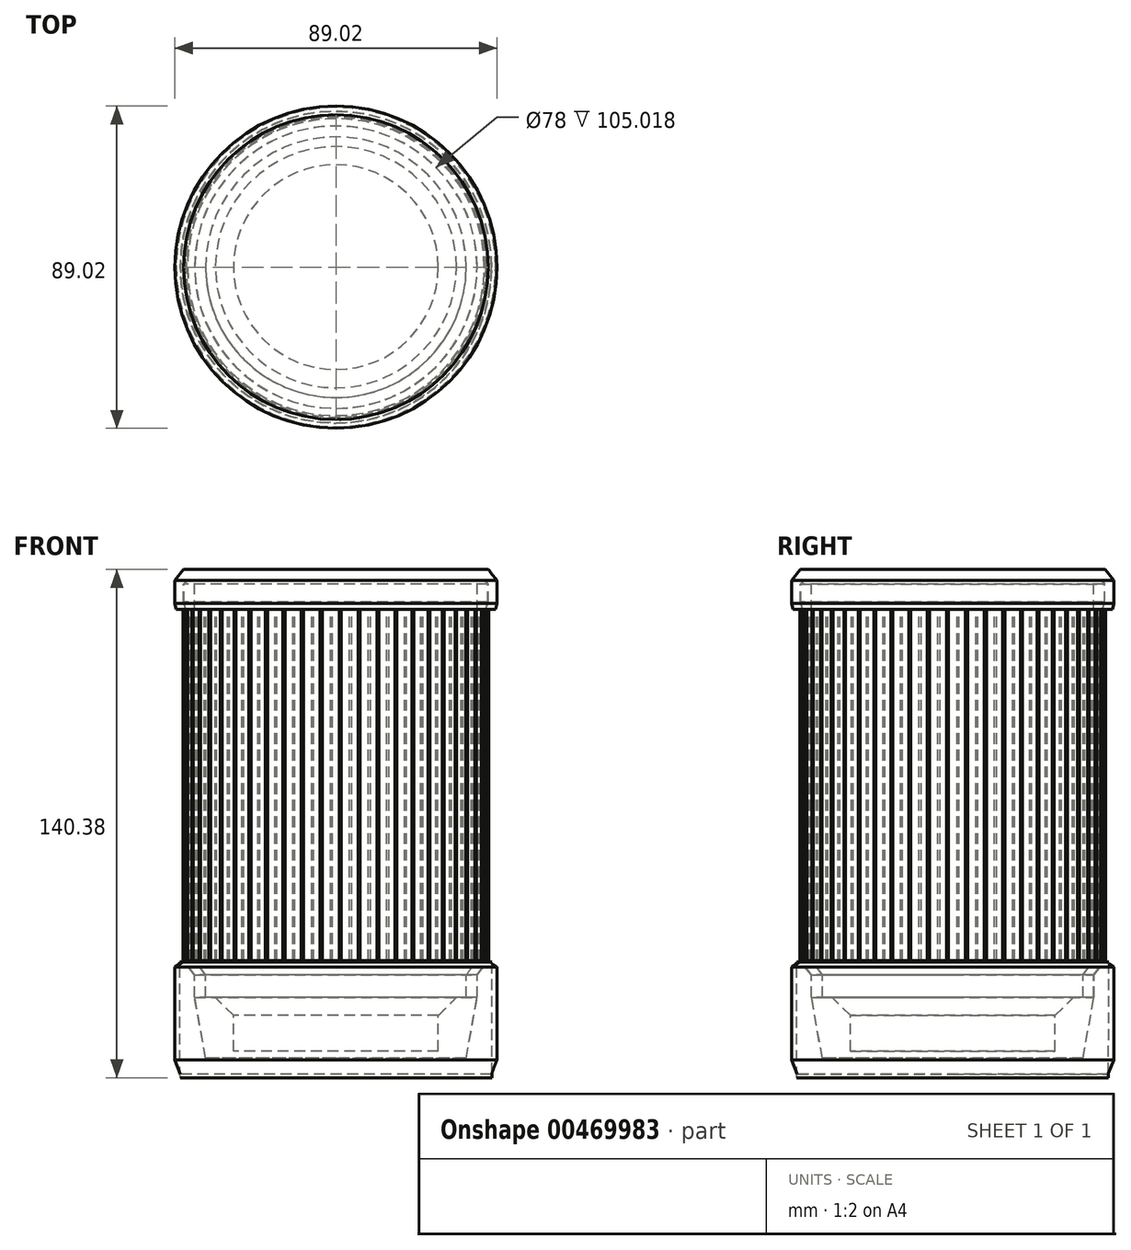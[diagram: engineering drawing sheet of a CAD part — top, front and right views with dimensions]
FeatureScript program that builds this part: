
annotation { "Feature Type Name" : "Feature", "Feature Type Description" : "" }
export const myFeature = defineFeature(function(context is Context, id is Id, definition is map)
    precondition{}
    {
        {
            var Q0;
            Q0=qCreatedBy(makeId("Front.planeOp"),FACE);
            var sketch = newSketch(context, id + "F0", { "sketchPlane" : qUnion([Q0])});
            skLineSegment(sketch, "E0", {"start": v(0, 0) * mm, "end": v(-28.3, 0) * mm});
            skLineSegment(sketch, "E1", {"start": v(-28.3, 0) * mm, "end": v(-28.3, 9.8) * mm});
            skLineSegment(sketch, "E2.bottom", {"start": v(0, 0) * mm, "end": v(-36, 0) * mm, "construction": true});
            skLineSegment(sketch, "E2.top", {"start": v(0, 21) * mm, "end": v(-36, 21) * mm, "construction": true});
            skLineSegment(sketch, "E2.left", {"start": v(0, 0) * mm, "end": v(0, 21) * mm, "construction": true});
            skLineSegment(sketch, "E2.right", {"start": v(-36, 0) * mm, "end": v(-36, 21) * mm, "construction": true});
            skLineSegment(sketch, "E3", {"start": v(-36, 21) * mm, "end": v(-36, 14.8) * mm});
            skLineSegment(sketch, "E4", {"start": v(-36, 14.8) * mm, "end": v(-33.3, 14.8) * mm});
            skLineSegment(sketch, "E5.bottom", {"start": v(0, 0) * mm, "end": v(-39, 0) * mm, "construction": true});
            skLineSegment(sketch, "E5.top", {"start": v(0, 130) * mm, "end": v(-39, 130) * mm, "construction": true});
            skLineSegment(sketch, "E5.left", {"start": v(0, 0) * mm, "end": v(0, 130) * mm, "construction": true});
            skLineSegment(sketch, "E5.right", {"start": v(-39, 0) * mm, "end": v(-39, 130) * mm, "construction": true});
            skLineSegment(sketch, "E6", {"start": v(-36, 21) * mm, "end": v(-39, 24.98) * mm});
            skLineSegment(sketch, "E7", {"start": v(-39, 24.98) * mm, "end": v(-39, 130) * mm});
            skLineSegment(sketch, "E8", {"start": v(-39, 130) * mm, "end": v(-42, 130) * mm});
            skLineSegment(sketch, "E9", {"start": v(-42, 130) * mm, "end": v(-42, 124) * mm});
            skLineSegment(sketch, "E10.bottom", {"start": v(-39, 130) * mm, "end": v(-41.4, 130) * mm, "construction": true});
            skLineSegment(sketch, "E10.top", {"start": v(-39, 122) * mm, "end": v(-41.4, 122) * mm, "construction": true});
            skLineSegment(sketch, "E10.left", {"start": v(-39, 130) * mm, "end": v(-39, 122) * mm, "construction": true});
            skLineSegment(sketch, "E10.right", {"start": v(-41.4, 130) * mm, "end": v(-41.4, 122) * mm, "construction": true});
            skLineSegment(sketch, "E11", {"start": v(-42, 124) * mm, "end": v(-41.4, 122) * mm});
            skLineSegment(sketch, "E12", {"start": v(-42, 122) * mm, "end": v(-42, 24.98) * mm});
            skLineSegment(sketch, "E13", {"start": v(-42, 24.98) * mm, "end": v(-39, 21) * mm});
            skLineSegment(sketch, "E14", {"start": v(-39, 21) * mm, "end": v(-39, 14.8) * mm});
            skLineSegment(sketch, "E15", {"start": v(-36, 17.9) * mm, "end": v(-39, 17.9) * mm, "construction": true});
            skLineSegment(sketch, "E16", {"start": v(0, 0) * mm, "end": v(0, -2) * mm});
            skLineSegment(sketch, "E17", {"start": v(0, -2) * mm, "end": v(-28.3, -2) * mm});
            skLineSegment(sketch, "E18", {"start": v(-39, 14.8) * mm, "end": v(-36, -2) * mm});
            skLineSegment(sketch, "E19", {"start": v(-36, -2) * mm, "end": v(-28.3, -2) * mm});
            skLineSegment(sketch, "E20", {"start": v(-33.3, 14.8) * mm, "end": v(-28.3, 9.8) * mm});
            skLineSegment(sketch, "E21", {"start": v(-42, 122) * mm, "end": v(-41.4, 122) * mm});
            skSolve(sketch);
        }
        {
            var Q0;
            Q0=makeQuery(id+"F0.imprint","IMPRINT",FACE,{"disambiguationData":[TD([[makeQuery(id+"F0.imprint","IMPRINT",EDGE,{"derivedFrom":sQuery(id+"F0.wireOp",EDGE,"E0")}),1.0]])]});
            var Q1;
            Q1=sQuery(id+"F0.wireOp",EDGE,"E16");
            revolve(context, id + "F1", {"entities" : qUnion([Q0]), "axis" : qUnion([Q1]), "revolveType" : RevolveType.FULL});
        }
        {
            var Q0;
            Q0=makeQuery(id+"F1.opRevolve","SWEPT_FACE",FACE,{"disambiguationData":[OSD([sQuery(id+"F0.wireOp",EDGE,"E21")])]});
            var sketch = newSketch(context, id + "F2", { "sketchPlane" : qUnion([Q0])});
            skCircle(sketch, "E22", {"center": v(36.08, -21.5) * mm, "radius": 0.29 * mm});
            skCircle(sketch, "E23.1.0", {"center": v(38.5, -16.8) * mm, "radius": 0.29 * mm});
            skCircle(sketch, "E23.2.0", {"center": v(40.3, -11.84) * mm, "radius": 0.29 * mm});
            skCircle(sketch, "E23.3.0", {"center": v(41.46, -6.7) * mm, "radius": 0.29 * mm});
            skCircle(sketch, "E23.4.0", {"center": v(41.97, -1.45) * mm, "radius": 0.29 * mm});
            skCircle(sketch, "E23.5.0", {"center": v(41.83, 3.82) * mm, "radius": 0.29 * mm});
            skCircle(sketch, "E23.6.0", {"center": v(41.02, 9.03) * mm, "radius": 0.29 * mm});
            skCircle(sketch, "E23.7.0", {"center": v(39.56, 14.1) * mm, "radius": 0.29 * mm});
            skCircle(sketch, "E23.8.0", {"center": v(37.48, 18.95) * mm, "radius": 0.29 * mm});
            skCircle(sketch, "E23.9.0", {"center": v(34.81, 23.5) * mm, "radius": 0.29 * mm});
            skCircle(sketch, "E23.10.0", {"center": v(31.6, 27.68) * mm, "radius": 0.29 * mm});
            skCircle(sketch, "E23.11.0", {"center": v(27.87, 31.42) * mm, "radius": 0.29 * mm});
            skCircle(sketch, "E23.12.0", {"center": v(23.72, 34.66) * mm, "radius": 0.29 * mm});
            skCircle(sketch, "E23.13.0", {"center": v(19.19, 37.36) * mm, "radius": 0.29 * mm});
            skCircle(sketch, "E23.14.0", {"center": v(14.35, 39.47) * mm, "radius": 0.29 * mm});
            skCircle(sketch, "E23.15.0", {"center": v(9.3, 40.96) * mm, "radius": 0.29 * mm});
            skCircle(sketch, "E23.16.0", {"center": v(4.08, 41.8) * mm, "radius": 0.29 * mm});
            skCircle(sketch, "E23.17.0", {"center": v(-1.19, 41.98) * mm, "radius": 0.29 * mm});
            skCircle(sketch, "E23.18.0", {"center": v(-6.44, 41.5) * mm, "radius": 0.29 * mm});
            skCircle(sketch, "E23.19.0", {"center": v(-11.6, 40.37) * mm, "radius": 0.29 * mm});
            skCircle(sketch, "E23.20.0", {"center": v(-16.56, 38.6) * mm, "radius": 0.29 * mm});
            skCircle(sketch, "E23.21.0", {"center": v(-21.27, 36.22) * mm, "radius": 0.29 * mm});
            skCircle(sketch, "E23.22.0", {"center": v(-25.64, 33.27) * mm, "radius": 0.29 * mm});
            skCircle(sketch, "E23.23.0", {"center": v(-29.6, 29.8) * mm, "radius": 0.29 * mm});
            skCircle(sketch, "E23.24.0", {"center": v(-33.1, 25.85) * mm, "radius": 0.29 * mm});
            skCircle(sketch, "E23.25.0", {"center": v(-36.08, 21.5) * mm, "radius": 0.29 * mm});
            skCircle(sketch, "E23.26.0", {"center": v(-38.5, 16.8) * mm, "radius": 0.29 * mm});
            skCircle(sketch, "E23.27.0", {"center": v(-40.3, 11.84) * mm, "radius": 0.29 * mm});
            skCircle(sketch, "E23.28.0", {"center": v(-41.46, 6.7) * mm, "radius": 0.29 * mm});
            skCircle(sketch, "E23.29.0", {"center": v(-41.97, 1.45) * mm, "radius": 0.29 * mm});
            skCircle(sketch, "E23.30.0", {"center": v(-41.83, -3.82) * mm, "radius": 0.29 * mm});
            skCircle(sketch, "E23.31.0", {"center": v(-41.02, -9.03) * mm, "radius": 0.29 * mm});
            skCircle(sketch, "E23.32.0", {"center": v(-39.56, -14.1) * mm, "radius": 0.29 * mm});
            skCircle(sketch, "E23.33.0", {"center": v(-37.48, -18.95) * mm, "radius": 0.29 * mm});
            skCircle(sketch, "E23.34.0", {"center": v(-34.81, -23.5) * mm, "radius": 0.29 * mm});
            skCircle(sketch, "E23.35.0", {"center": v(-31.6, -27.68) * mm, "radius": 0.29 * mm});
            skCircle(sketch, "E23.36.0", {"center": v(-27.87, -31.42) * mm, "radius": 0.29 * mm});
            skCircle(sketch, "E23.37.0", {"center": v(-23.72, -34.66) * mm, "radius": 0.29 * mm});
            skCircle(sketch, "E23.38.0", {"center": v(-19.19, -37.36) * mm, "radius": 0.29 * mm});
            skCircle(sketch, "E23.39.0", {"center": v(-14.35, -39.47) * mm, "radius": 0.29 * mm});
            skCircle(sketch, "E23.40.0", {"center": v(-9.3, -40.96) * mm, "radius": 0.29 * mm});
            skCircle(sketch, "E23.41.0", {"center": v(-4.08, -41.8) * mm, "radius": 0.29 * mm});
            skCircle(sketch, "E23.42.0", {"center": v(1.19, -41.98) * mm, "radius": 0.29 * mm});
            skCircle(sketch, "E23.43.0", {"center": v(6.44, -41.5) * mm, "radius": 0.29 * mm});
            skCircle(sketch, "E23.44.0", {"center": v(11.6, -40.37) * mm, "radius": 0.29 * mm});
            skCircle(sketch, "E23.45.0", {"center": v(16.56, -38.6) * mm, "radius": 0.29 * mm});
            skCircle(sketch, "E23.46.0", {"center": v(21.27, -36.22) * mm, "radius": 0.29 * mm});
            skCircle(sketch, "E23.47.0", {"center": v(25.64, -33.27) * mm, "radius": 0.29 * mm});
            skCircle(sketch, "E23.48.0", {"center": v(29.6, -29.8) * mm, "radius": 0.29 * mm});
            skCircle(sketch, "E23.49.0", {"center": v(33.1, -25.85) * mm, "radius": 0.29 * mm});
            skPoint(sketch, "E23.center", {"position": v(0, 0) * mm});
            skSolve(sketch);
        }
        {
            var Q0;
            {var subQ0=sQuery(id+"F2.wireOp",EDGE,"E23.46.0");var subQ1=makeQuery(id+"F1.opRevolve","SWEPT_EDGE",EDGE,{"disambiguationData":[OSD([sQuery(id+"F0.wireOp",EDGE,"E12"),sQuery(id+"F0.wireOp",EDGE,"E21")])]});var subQ2=makeQuery(id+"F2.imprint","INTERSECT",VERTEX,{"disambiguationData":[OD(0.0)],"derivedFrom":[subQ1,subQ0]});Q0=makeQuery(id+"F2.imprint","IMPRINT",FACE,{"disambiguationData":[TD([[makeQuery(id+"F2.imprint","IMPRINT",EDGE,{"disambiguationData":[TD([[subQ2,1.0]])],"derivedFrom":subQ0}),1.0]])]});}
            var Q1;
            {var subQ0=sQuery(id+"F2.wireOp",EDGE,"E23.46.0");var subQ1=makeQuery(id+"F1.opRevolve","SWEPT_EDGE",EDGE,{"disambiguationData":[OSD([sQuery(id+"F0.wireOp",EDGE,"E12"),sQuery(id+"F0.wireOp",EDGE,"E21")])]});var subQ2=makeQuery(id+"F2.imprint","INTERSECT",VERTEX,{"disambiguationData":[OD(0.0)],"derivedFrom":[subQ1,subQ0]});Q1=makeQuery(id+"F2.imprint","IMPRINT",FACE,{"disambiguationData":[TD([[makeQuery(id+"F2.imprint","IMPRINT",EDGE,{"disambiguationData":[TD([[subQ2,-1.0]])],"derivedFrom":subQ0}),1.0]])]});}
            var Q2;
            {var subQ0=sQuery(id+"F2.wireOp",EDGE,"E23.47.0");var subQ1=makeQuery(id+"F1.opRevolve","SWEPT_EDGE",EDGE,{"disambiguationData":[OSD([sQuery(id+"F0.wireOp",EDGE,"E12"),sQuery(id+"F0.wireOp",EDGE,"E21")])]});var subQ2=makeQuery(id+"F2.imprint","INTERSECT",VERTEX,{"disambiguationData":[OD(0.0)],"derivedFrom":[subQ1,subQ0]});Q2=makeQuery(id+"F2.imprint","IMPRINT",FACE,{"disambiguationData":[TD([[makeQuery(id+"F2.imprint","IMPRINT",EDGE,{"disambiguationData":[TD([[subQ2,-1.0]])],"derivedFrom":subQ0}),1.0]])]});}
            var Q3;
            {var subQ0=sQuery(id+"F2.wireOp",EDGE,"E23.47.0");var subQ1=makeQuery(id+"F1.opRevolve","SWEPT_EDGE",EDGE,{"disambiguationData":[OSD([sQuery(id+"F0.wireOp",EDGE,"E12"),sQuery(id+"F0.wireOp",EDGE,"E21")])]});var subQ2=makeQuery(id+"F2.imprint","INTERSECT",VERTEX,{"disambiguationData":[OD(0.0)],"derivedFrom":[subQ1,subQ0]});Q3=makeQuery(id+"F2.imprint","IMPRINT",FACE,{"disambiguationData":[TD([[makeQuery(id+"F2.imprint","IMPRINT",EDGE,{"disambiguationData":[TD([[subQ2,1.0]])],"derivedFrom":subQ0}),1.0]])]});}
            var Q4;
            {var subQ0=sQuery(id+"F2.wireOp",EDGE,"E23.48.0");var subQ1=makeQuery(id+"F1.opRevolve","SWEPT_EDGE",EDGE,{"disambiguationData":[OSD([sQuery(id+"F0.wireOp",EDGE,"E12"),sQuery(id+"F0.wireOp",EDGE,"E21")])]});var subQ2=makeQuery(id+"F2.imprint","INTERSECT",VERTEX,{"disambiguationData":[OD(0.0)],"derivedFrom":[subQ1,subQ0]});Q4=makeQuery(id+"F2.imprint","IMPRINT",FACE,{"disambiguationData":[TD([[makeQuery(id+"F2.imprint","IMPRINT",EDGE,{"disambiguationData":[TD([[subQ2,-1.0]])],"derivedFrom":subQ0}),1.0]])]});}
            var Q5;
            {var subQ0=sQuery(id+"F2.wireOp",EDGE,"E23.48.0");var subQ1=makeQuery(id+"F1.opRevolve","SWEPT_EDGE",EDGE,{"disambiguationData":[OSD([sQuery(id+"F0.wireOp",EDGE,"E12"),sQuery(id+"F0.wireOp",EDGE,"E21")])]});var subQ2=makeQuery(id+"F2.imprint","INTERSECT",VERTEX,{"disambiguationData":[OD(0.0)],"derivedFrom":[subQ1,subQ0]});Q5=makeQuery(id+"F2.imprint","IMPRINT",FACE,{"disambiguationData":[TD([[makeQuery(id+"F2.imprint","IMPRINT",EDGE,{"disambiguationData":[TD([[subQ2,1.0]])],"derivedFrom":subQ0}),1.0]])]});}
            var Q6;
            {var subQ0=sQuery(id+"F2.wireOp",EDGE,"E23.49.0");var subQ1=makeQuery(id+"F1.opRevolve","SWEPT_EDGE",EDGE,{"disambiguationData":[OSD([sQuery(id+"F0.wireOp",EDGE,"E12"),sQuery(id+"F0.wireOp",EDGE,"E21")])]});var subQ2=makeQuery(id+"F2.imprint","INTERSECT",VERTEX,{"disambiguationData":[OD(0.0)],"derivedFrom":[subQ1,subQ0]});Q6=makeQuery(id+"F2.imprint","IMPRINT",FACE,{"disambiguationData":[TD([[makeQuery(id+"F2.imprint","IMPRINT",EDGE,{"disambiguationData":[TD([[subQ2,-1.0]])],"derivedFrom":subQ0}),1.0]])]});}
            var Q7;
            {var subQ0=sQuery(id+"F2.wireOp",EDGE,"E23.49.0");var subQ1=makeQuery(id+"F1.opRevolve","SWEPT_EDGE",EDGE,{"disambiguationData":[OSD([sQuery(id+"F0.wireOp",EDGE,"E12"),sQuery(id+"F0.wireOp",EDGE,"E21")])]});var subQ2=makeQuery(id+"F2.imprint","INTERSECT",VERTEX,{"disambiguationData":[OD(0.0)],"derivedFrom":[subQ1,subQ0]});Q7=makeQuery(id+"F2.imprint","IMPRINT",FACE,{"disambiguationData":[TD([[makeQuery(id+"F2.imprint","IMPRINT",EDGE,{"disambiguationData":[TD([[subQ2,1.0]])],"derivedFrom":subQ0}),1.0]])]});}
            var Q8;
            {var subQ0=sQuery(id+"F2.wireOp",EDGE,"E22");var subQ1=makeQuery(id+"F1.opRevolve","SWEPT_EDGE",EDGE,{"disambiguationData":[OSD([sQuery(id+"F0.wireOp",EDGE,"E12"),sQuery(id+"F0.wireOp",EDGE,"E21")])]});var subQ2=makeQuery(id+"F2.imprint","INTERSECT",VERTEX,{"disambiguationData":[OD(0.0)],"derivedFrom":[subQ1,subQ0]});Q8=makeQuery(id+"F2.imprint","IMPRINT",FACE,{"disambiguationData":[TD([[makeQuery(id+"F2.imprint","IMPRINT",EDGE,{"disambiguationData":[TD([[subQ2,-1.0]])],"derivedFrom":subQ0}),1.0]])]});}
            var Q9;
            {var subQ0=sQuery(id+"F2.wireOp",EDGE,"E22");var subQ1=makeQuery(id+"F1.opRevolve","SWEPT_EDGE",EDGE,{"disambiguationData":[OSD([sQuery(id+"F0.wireOp",EDGE,"E12"),sQuery(id+"F0.wireOp",EDGE,"E21")])]});var subQ2=makeQuery(id+"F2.imprint","INTERSECT",VERTEX,{"disambiguationData":[OD(0.0)],"derivedFrom":[subQ1,subQ0]});Q9=makeQuery(id+"F2.imprint","IMPRINT",FACE,{"disambiguationData":[TD([[makeQuery(id+"F2.imprint","IMPRINT",EDGE,{"disambiguationData":[TD([[subQ2,1.0]])],"derivedFrom":subQ0}),1.0]])]});}
            var Q10;
            {var subQ0=sQuery(id+"F2.wireOp",EDGE,"E23.1.0");var subQ1=makeQuery(id+"F1.opRevolve","SWEPT_EDGE",EDGE,{"disambiguationData":[OSD([sQuery(id+"F0.wireOp",EDGE,"E12"),sQuery(id+"F0.wireOp",EDGE,"E21")])]});var subQ2=makeQuery(id+"F2.imprint","INTERSECT",VERTEX,{"disambiguationData":[OD(0.0)],"derivedFrom":[subQ1,subQ0]});Q10=makeQuery(id+"F2.imprint","IMPRINT",FACE,{"disambiguationData":[TD([[makeQuery(id+"F2.imprint","IMPRINT",EDGE,{"disambiguationData":[TD([[subQ2,-1.0]])],"derivedFrom":subQ0}),1.0]])]});}
            var Q11;
            {var subQ0=sQuery(id+"F2.wireOp",EDGE,"E23.1.0");var subQ1=makeQuery(id+"F1.opRevolve","SWEPT_EDGE",EDGE,{"disambiguationData":[OSD([sQuery(id+"F0.wireOp",EDGE,"E12"),sQuery(id+"F0.wireOp",EDGE,"E21")])]});var subQ2=makeQuery(id+"F2.imprint","INTERSECT",VERTEX,{"disambiguationData":[OD(0.0)],"derivedFrom":[subQ1,subQ0]});Q11=makeQuery(id+"F2.imprint","IMPRINT",FACE,{"disambiguationData":[TD([[makeQuery(id+"F2.imprint","IMPRINT",EDGE,{"disambiguationData":[TD([[subQ2,1.0]])],"derivedFrom":subQ0}),1.0]])]});}
            var Q12;
            {var subQ0=sQuery(id+"F2.wireOp",EDGE,"E23.2.0");var subQ1=makeQuery(id+"F1.opRevolve","SWEPT_EDGE",EDGE,{"disambiguationData":[OSD([sQuery(id+"F0.wireOp",EDGE,"E12"),sQuery(id+"F0.wireOp",EDGE,"E21")])]});var subQ2=makeQuery(id+"F2.imprint","INTERSECT",VERTEX,{"disambiguationData":[OD(0.0)],"derivedFrom":[subQ1,subQ0]});Q12=makeQuery(id+"F2.imprint","IMPRINT",FACE,{"disambiguationData":[TD([[makeQuery(id+"F2.imprint","IMPRINT",EDGE,{"disambiguationData":[TD([[subQ2,1.0]])],"derivedFrom":subQ0}),1.0]])]});}
            var Q13;
            {var subQ0=sQuery(id+"F2.wireOp",EDGE,"E23.2.0");var subQ1=makeQuery(id+"F1.opRevolve","SWEPT_EDGE",EDGE,{"disambiguationData":[OSD([sQuery(id+"F0.wireOp",EDGE,"E12"),sQuery(id+"F0.wireOp",EDGE,"E21")])]});var subQ2=makeQuery(id+"F2.imprint","INTERSECT",VERTEX,{"disambiguationData":[OD(0.0)],"derivedFrom":[subQ1,subQ0]});Q13=makeQuery(id+"F2.imprint","IMPRINT",FACE,{"disambiguationData":[TD([[makeQuery(id+"F2.imprint","IMPRINT",EDGE,{"disambiguationData":[TD([[subQ2,-1.0]])],"derivedFrom":subQ0}),1.0]])]});}
            var Q14;
            {var subQ0=sQuery(id+"F2.wireOp",EDGE,"E23.3.0");var subQ1=makeQuery(id+"F1.opRevolve","SWEPT_EDGE",EDGE,{"disambiguationData":[OSD([sQuery(id+"F0.wireOp",EDGE,"E12"),sQuery(id+"F0.wireOp",EDGE,"E21")])]});var subQ2=makeQuery(id+"F2.imprint","INTERSECT",VERTEX,{"disambiguationData":[OD(0.0)],"derivedFrom":[subQ1,subQ0]});Q14=makeQuery(id+"F2.imprint","IMPRINT",FACE,{"disambiguationData":[TD([[makeQuery(id+"F2.imprint","IMPRINT",EDGE,{"disambiguationData":[TD([[subQ2,1.0]])],"derivedFrom":subQ0}),1.0]])]});}
            var Q15;
            {var subQ0=sQuery(id+"F2.wireOp",EDGE,"E23.3.0");var subQ1=makeQuery(id+"F1.opRevolve","SWEPT_EDGE",EDGE,{"disambiguationData":[OSD([sQuery(id+"F0.wireOp",EDGE,"E12"),sQuery(id+"F0.wireOp",EDGE,"E21")])]});var subQ2=makeQuery(id+"F2.imprint","INTERSECT",VERTEX,{"disambiguationData":[OD(0.0)],"derivedFrom":[subQ1,subQ0]});Q15=makeQuery(id+"F2.imprint","IMPRINT",FACE,{"disambiguationData":[TD([[makeQuery(id+"F2.imprint","IMPRINT",EDGE,{"disambiguationData":[TD([[subQ2,-1.0]])],"derivedFrom":subQ0}),1.0]])]});}
            var Q16;
            {var subQ0=sQuery(id+"F2.wireOp",EDGE,"E23.4.0");var subQ1=makeQuery(id+"F1.opRevolve","SWEPT_EDGE",EDGE,{"disambiguationData":[OSD([sQuery(id+"F0.wireOp",EDGE,"E12"),sQuery(id+"F0.wireOp",EDGE,"E21")])]});var subQ2=makeQuery(id+"F2.imprint","INTERSECT",VERTEX,{"disambiguationData":[OD(0.0)],"derivedFrom":[subQ1,subQ0]});Q16=makeQuery(id+"F2.imprint","IMPRINT",FACE,{"disambiguationData":[TD([[makeQuery(id+"F2.imprint","IMPRINT",EDGE,{"disambiguationData":[TD([[subQ2,-1.0]])],"derivedFrom":subQ0}),1.0]])]});}
            var Q17;
            {var subQ0=sQuery(id+"F2.wireOp",EDGE,"E23.5.0");var subQ1=makeQuery(id+"F1.opRevolve","SWEPT_EDGE",EDGE,{"disambiguationData":[OSD([sQuery(id+"F0.wireOp",EDGE,"E12"),sQuery(id+"F0.wireOp",EDGE,"E21")])]});var subQ2=makeQuery(id+"F2.imprint","INTERSECT",VERTEX,{"disambiguationData":[OD(0.0)],"derivedFrom":[subQ1,subQ0]});Q17=makeQuery(id+"F2.imprint","IMPRINT",FACE,{"disambiguationData":[TD([[makeQuery(id+"F2.imprint","IMPRINT",EDGE,{"disambiguationData":[TD([[subQ2,-1.0]])],"derivedFrom":subQ0}),1.0]])]});}
            var Q18;
            {var subQ0=sQuery(id+"F2.wireOp",EDGE,"E23.9.0");var subQ1=makeQuery(id+"F1.opRevolve","SWEPT_EDGE",EDGE,{"disambiguationData":[OSD([sQuery(id+"F0.wireOp",EDGE,"E12"),sQuery(id+"F0.wireOp",EDGE,"E21")])]});var subQ2=makeQuery(id+"F2.imprint","INTERSECT",VERTEX,{"disambiguationData":[OD(0.0)],"derivedFrom":[subQ1,subQ0]});Q18=makeQuery(id+"F2.imprint","IMPRINT",FACE,{"disambiguationData":[TD([[makeQuery(id+"F2.imprint","IMPRINT",EDGE,{"disambiguationData":[TD([[subQ2,1.0]])],"derivedFrom":subQ0}),1.0]])]});}
            var Q19;
            {var subQ0=sQuery(id+"F2.wireOp",EDGE,"E23.8.0");var subQ1=makeQuery(id+"F1.opRevolve","SWEPT_EDGE",EDGE,{"disambiguationData":[OSD([sQuery(id+"F0.wireOp",EDGE,"E12"),sQuery(id+"F0.wireOp",EDGE,"E21")])]});var subQ2=makeQuery(id+"F2.imprint","INTERSECT",VERTEX,{"disambiguationData":[OD(0.0)],"derivedFrom":[subQ1,subQ0]});Q19=makeQuery(id+"F2.imprint","IMPRINT",FACE,{"disambiguationData":[TD([[makeQuery(id+"F2.imprint","IMPRINT",EDGE,{"disambiguationData":[TD([[subQ2,1.0]])],"derivedFrom":subQ0}),1.0]])]});}
            var Q20;
            {var subQ0=sQuery(id+"F2.wireOp",EDGE,"E23.7.0");var subQ1=makeQuery(id+"F1.opRevolve","SWEPT_EDGE",EDGE,{"disambiguationData":[OSD([sQuery(id+"F0.wireOp",EDGE,"E12"),sQuery(id+"F0.wireOp",EDGE,"E21")])]});var subQ2=makeQuery(id+"F2.imprint","INTERSECT",VERTEX,{"disambiguationData":[OD(0.0)],"derivedFrom":[subQ1,subQ0]});Q20=makeQuery(id+"F2.imprint","IMPRINT",FACE,{"disambiguationData":[TD([[makeQuery(id+"F2.imprint","IMPRINT",EDGE,{"disambiguationData":[TD([[subQ2,-1.0]])],"derivedFrom":subQ0}),1.0]])]});}
            var Q21;
            {var subQ0=sQuery(id+"F2.wireOp",EDGE,"E23.6.0");var subQ1=makeQuery(id+"F1.opRevolve","SWEPT_EDGE",EDGE,{"disambiguationData":[OSD([sQuery(id+"F0.wireOp",EDGE,"E12"),sQuery(id+"F0.wireOp",EDGE,"E21")])]});var subQ2=makeQuery(id+"F2.imprint","INTERSECT",VERTEX,{"disambiguationData":[OD(0.0)],"derivedFrom":[subQ1,subQ0]});Q21=makeQuery(id+"F2.imprint","IMPRINT",FACE,{"disambiguationData":[TD([[makeQuery(id+"F2.imprint","IMPRINT",EDGE,{"disambiguationData":[TD([[subQ2,-1.0]])],"derivedFrom":subQ0}),1.0]])]});}
            var Q22;
            {var subQ0=sQuery(id+"F2.wireOp",EDGE,"E23.7.0");var subQ1=makeQuery(id+"F1.opRevolve","SWEPT_EDGE",EDGE,{"disambiguationData":[OSD([sQuery(id+"F0.wireOp",EDGE,"E12"),sQuery(id+"F0.wireOp",EDGE,"E21")])]});var subQ2=makeQuery(id+"F2.imprint","INTERSECT",VERTEX,{"disambiguationData":[OD(0.0)],"derivedFrom":[subQ1,subQ0]});Q22=makeQuery(id+"F2.imprint","IMPRINT",FACE,{"disambiguationData":[TD([[makeQuery(id+"F2.imprint","IMPRINT",EDGE,{"disambiguationData":[TD([[subQ2,1.0]])],"derivedFrom":subQ0}),1.0]])]});}
            var Q23;
            {var subQ0=sQuery(id+"F2.wireOp",EDGE,"E23.8.0");var subQ1=makeQuery(id+"F1.opRevolve","SWEPT_EDGE",EDGE,{"disambiguationData":[OSD([sQuery(id+"F0.wireOp",EDGE,"E12"),sQuery(id+"F0.wireOp",EDGE,"E21")])]});var subQ2=makeQuery(id+"F2.imprint","INTERSECT",VERTEX,{"disambiguationData":[OD(0.0)],"derivedFrom":[subQ1,subQ0]});Q23=makeQuery(id+"F2.imprint","IMPRINT",FACE,{"disambiguationData":[TD([[makeQuery(id+"F2.imprint","IMPRINT",EDGE,{"disambiguationData":[TD([[subQ2,-1.0]])],"derivedFrom":subQ0}),1.0]])]});}
            var Q24;
            {var subQ0=sQuery(id+"F2.wireOp",EDGE,"E23.6.0");var subQ1=makeQuery(id+"F1.opRevolve","SWEPT_EDGE",EDGE,{"disambiguationData":[OSD([sQuery(id+"F0.wireOp",EDGE,"E12"),sQuery(id+"F0.wireOp",EDGE,"E21")])]});var subQ2=makeQuery(id+"F2.imprint","INTERSECT",VERTEX,{"disambiguationData":[OD(0.0)],"derivedFrom":[subQ1,subQ0]});Q24=makeQuery(id+"F2.imprint","IMPRINT",FACE,{"disambiguationData":[TD([[makeQuery(id+"F2.imprint","IMPRINT",EDGE,{"disambiguationData":[TD([[subQ2,1.0]])],"derivedFrom":subQ0}),1.0]])]});}
            var Q25;
            {var subQ0=sQuery(id+"F2.wireOp",EDGE,"E23.5.0");var subQ1=makeQuery(id+"F1.opRevolve","SWEPT_EDGE",EDGE,{"disambiguationData":[OSD([sQuery(id+"F0.wireOp",EDGE,"E12"),sQuery(id+"F0.wireOp",EDGE,"E21")])]});var subQ2=makeQuery(id+"F2.imprint","INTERSECT",VERTEX,{"disambiguationData":[OD(0.0)],"derivedFrom":[subQ1,subQ0]});Q25=makeQuery(id+"F2.imprint","IMPRINT",FACE,{"disambiguationData":[TD([[makeQuery(id+"F2.imprint","IMPRINT",EDGE,{"disambiguationData":[TD([[subQ2,1.0]])],"derivedFrom":subQ0}),1.0]])]});}
            var Q26;
            {var subQ0=sQuery(id+"F2.wireOp",EDGE,"E23.4.0");var subQ1=makeQuery(id+"F1.opRevolve","SWEPT_EDGE",EDGE,{"disambiguationData":[OSD([sQuery(id+"F0.wireOp",EDGE,"E12"),sQuery(id+"F0.wireOp",EDGE,"E21")])]});var subQ2=makeQuery(id+"F2.imprint","INTERSECT",VERTEX,{"disambiguationData":[OD(0.0)],"derivedFrom":[subQ1,subQ0]});Q26=makeQuery(id+"F2.imprint","IMPRINT",FACE,{"disambiguationData":[TD([[makeQuery(id+"F2.imprint","IMPRINT",EDGE,{"disambiguationData":[TD([[subQ2,1.0]])],"derivedFrom":subQ0}),1.0]])]});}
            var Q27;
            {var subQ0=sQuery(id+"F2.wireOp",EDGE,"E23.9.0");var subQ1=makeQuery(id+"F1.opRevolve","SWEPT_EDGE",EDGE,{"disambiguationData":[OSD([sQuery(id+"F0.wireOp",EDGE,"E12"),sQuery(id+"F0.wireOp",EDGE,"E21")])]});var subQ2=makeQuery(id+"F2.imprint","INTERSECT",VERTEX,{"disambiguationData":[OD(0.0)],"derivedFrom":[subQ1,subQ0]});Q27=makeQuery(id+"F2.imprint","IMPRINT",FACE,{"disambiguationData":[TD([[makeQuery(id+"F2.imprint","IMPRINT",EDGE,{"disambiguationData":[TD([[subQ2,-1.0]])],"derivedFrom":subQ0}),1.0]])]});}
            var Q28;
            {var subQ0=sQuery(id+"F2.wireOp",EDGE,"E23.11.0");var subQ1=makeQuery(id+"F1.opRevolve","SWEPT_EDGE",EDGE,{"disambiguationData":[OSD([sQuery(id+"F0.wireOp",EDGE,"E12"),sQuery(id+"F0.wireOp",EDGE,"E21")])]});var subQ2=makeQuery(id+"F2.imprint","INTERSECT",VERTEX,{"disambiguationData":[OD(0.0)],"derivedFrom":[subQ1,subQ0]});Q28=makeQuery(id+"F2.imprint","IMPRINT",FACE,{"disambiguationData":[TD([[makeQuery(id+"F2.imprint","IMPRINT",EDGE,{"disambiguationData":[TD([[subQ2,1.0]])],"derivedFrom":subQ0}),1.0]])]});}
            var Q29;
            {var subQ0=sQuery(id+"F2.wireOp",EDGE,"E23.11.0");var subQ1=makeQuery(id+"F1.opRevolve","SWEPT_EDGE",EDGE,{"disambiguationData":[OSD([sQuery(id+"F0.wireOp",EDGE,"E12"),sQuery(id+"F0.wireOp",EDGE,"E21")])]});var subQ2=makeQuery(id+"F2.imprint","INTERSECT",VERTEX,{"disambiguationData":[OD(0.0)],"derivedFrom":[subQ1,subQ0]});Q29=makeQuery(id+"F2.imprint","IMPRINT",FACE,{"disambiguationData":[TD([[makeQuery(id+"F2.imprint","IMPRINT",EDGE,{"disambiguationData":[TD([[subQ2,-1.0]])],"derivedFrom":subQ0}),1.0]])]});}
            var Q30;
            {var subQ0=sQuery(id+"F2.wireOp",EDGE,"E23.10.0");var subQ1=makeQuery(id+"F1.opRevolve","SWEPT_EDGE",EDGE,{"disambiguationData":[OSD([sQuery(id+"F0.wireOp",EDGE,"E12"),sQuery(id+"F0.wireOp",EDGE,"E21")])]});var subQ2=makeQuery(id+"F2.imprint","INTERSECT",VERTEX,{"disambiguationData":[OD(0.0)],"derivedFrom":[subQ1,subQ0]});Q30=makeQuery(id+"F2.imprint","IMPRINT",FACE,{"disambiguationData":[TD([[makeQuery(id+"F2.imprint","IMPRINT",EDGE,{"disambiguationData":[TD([[subQ2,-1.0]])],"derivedFrom":subQ0}),1.0]])]});}
            var Q31;
            {var subQ0=sQuery(id+"F2.wireOp",EDGE,"E23.10.0");var subQ1=makeQuery(id+"F1.opRevolve","SWEPT_EDGE",EDGE,{"disambiguationData":[OSD([sQuery(id+"F0.wireOp",EDGE,"E12"),sQuery(id+"F0.wireOp",EDGE,"E21")])]});var subQ2=makeQuery(id+"F2.imprint","INTERSECT",VERTEX,{"disambiguationData":[OD(0.0)],"derivedFrom":[subQ1,subQ0]});Q31=makeQuery(id+"F2.imprint","IMPRINT",FACE,{"disambiguationData":[TD([[makeQuery(id+"F2.imprint","IMPRINT",EDGE,{"disambiguationData":[TD([[subQ2,1.0]])],"derivedFrom":subQ0}),1.0]])]});}
            var Q32;
            {var subQ0=sQuery(id+"F2.wireOp",EDGE,"E23.12.0");var subQ1=makeQuery(id+"F1.opRevolve","SWEPT_EDGE",EDGE,{"disambiguationData":[OSD([sQuery(id+"F0.wireOp",EDGE,"E12"),sQuery(id+"F0.wireOp",EDGE,"E21")])]});var subQ2=makeQuery(id+"F2.imprint","INTERSECT",VERTEX,{"disambiguationData":[OD(0.0)],"derivedFrom":[subQ1,subQ0]});Q32=makeQuery(id+"F2.imprint","IMPRINT",FACE,{"disambiguationData":[TD([[makeQuery(id+"F2.imprint","IMPRINT",EDGE,{"disambiguationData":[TD([[subQ2,-1.0]])],"derivedFrom":subQ0}),1.0]])]});}
            var Q33;
            {var subQ0=sQuery(id+"F2.wireOp",EDGE,"E23.12.0");var subQ1=makeQuery(id+"F1.opRevolve","SWEPT_EDGE",EDGE,{"disambiguationData":[OSD([sQuery(id+"F0.wireOp",EDGE,"E12"),sQuery(id+"F0.wireOp",EDGE,"E21")])]});var subQ2=makeQuery(id+"F2.imprint","INTERSECT",VERTEX,{"disambiguationData":[OD(0.0)],"derivedFrom":[subQ1,subQ0]});Q33=makeQuery(id+"F2.imprint","IMPRINT",FACE,{"disambiguationData":[TD([[makeQuery(id+"F2.imprint","IMPRINT",EDGE,{"disambiguationData":[TD([[subQ2,1.0]])],"derivedFrom":subQ0}),1.0]])]});}
            var Q34;
            {var subQ0=sQuery(id+"F2.wireOp",EDGE,"E23.13.0");var subQ1=makeQuery(id+"F1.opRevolve","SWEPT_EDGE",EDGE,{"disambiguationData":[OSD([sQuery(id+"F0.wireOp",EDGE,"E12"),sQuery(id+"F0.wireOp",EDGE,"E21")])]});var subQ2=makeQuery(id+"F2.imprint","INTERSECT",VERTEX,{"disambiguationData":[OD(0.0)],"derivedFrom":[subQ1,subQ0]});Q34=makeQuery(id+"F2.imprint","IMPRINT",FACE,{"disambiguationData":[TD([[makeQuery(id+"F2.imprint","IMPRINT",EDGE,{"disambiguationData":[TD([[subQ2,-1.0]])],"derivedFrom":subQ0}),1.0]])]});}
            var Q35;
            {var subQ0=sQuery(id+"F2.wireOp",EDGE,"E23.13.0");var subQ1=makeQuery(id+"F1.opRevolve","SWEPT_EDGE",EDGE,{"disambiguationData":[OSD([sQuery(id+"F0.wireOp",EDGE,"E12"),sQuery(id+"F0.wireOp",EDGE,"E21")])]});var subQ2=makeQuery(id+"F2.imprint","INTERSECT",VERTEX,{"disambiguationData":[OD(0.0)],"derivedFrom":[subQ1,subQ0]});Q35=makeQuery(id+"F2.imprint","IMPRINT",FACE,{"disambiguationData":[TD([[makeQuery(id+"F2.imprint","IMPRINT",EDGE,{"disambiguationData":[TD([[subQ2,1.0]])],"derivedFrom":subQ0}),1.0]])]});}
            var Q36;
            {var subQ0=sQuery(id+"F2.wireOp",EDGE,"E23.14.0");var subQ1=makeQuery(id+"F1.opRevolve","SWEPT_EDGE",EDGE,{"disambiguationData":[OSD([sQuery(id+"F0.wireOp",EDGE,"E12"),sQuery(id+"F0.wireOp",EDGE,"E21")])]});var subQ2=makeQuery(id+"F2.imprint","INTERSECT",VERTEX,{"disambiguationData":[OD(0.0)],"derivedFrom":[subQ1,subQ0]});Q36=makeQuery(id+"F2.imprint","IMPRINT",FACE,{"disambiguationData":[TD([[makeQuery(id+"F2.imprint","IMPRINT",EDGE,{"disambiguationData":[TD([[subQ2,-1.0]])],"derivedFrom":subQ0}),1.0]])]});}
            var Q37;
            {var subQ0=sQuery(id+"F2.wireOp",EDGE,"E23.14.0");var subQ1=makeQuery(id+"F1.opRevolve","SWEPT_EDGE",EDGE,{"disambiguationData":[OSD([sQuery(id+"F0.wireOp",EDGE,"E12"),sQuery(id+"F0.wireOp",EDGE,"E21")])]});var subQ2=makeQuery(id+"F2.imprint","INTERSECT",VERTEX,{"disambiguationData":[OD(0.0)],"derivedFrom":[subQ1,subQ0]});Q37=makeQuery(id+"F2.imprint","IMPRINT",FACE,{"disambiguationData":[TD([[makeQuery(id+"F2.imprint","IMPRINT",EDGE,{"disambiguationData":[TD([[subQ2,1.0]])],"derivedFrom":subQ0}),1.0]])]});}
            var Q38;
            {var subQ0=sQuery(id+"F2.wireOp",EDGE,"E23.15.0");var subQ1=makeQuery(id+"F1.opRevolve","SWEPT_EDGE",EDGE,{"disambiguationData":[OSD([sQuery(id+"F0.wireOp",EDGE,"E12"),sQuery(id+"F0.wireOp",EDGE,"E21")])]});var subQ2=makeQuery(id+"F2.imprint","INTERSECT",VERTEX,{"disambiguationData":[OD(0.0)],"derivedFrom":[subQ1,subQ0]});Q38=makeQuery(id+"F2.imprint","IMPRINT",FACE,{"disambiguationData":[TD([[makeQuery(id+"F2.imprint","IMPRINT",EDGE,{"disambiguationData":[TD([[subQ2,-1.0]])],"derivedFrom":subQ0}),1.0]])]});}
            var Q39;
            {var subQ0=sQuery(id+"F2.wireOp",EDGE,"E23.15.0");var subQ1=makeQuery(id+"F1.opRevolve","SWEPT_EDGE",EDGE,{"disambiguationData":[OSD([sQuery(id+"F0.wireOp",EDGE,"E12"),sQuery(id+"F0.wireOp",EDGE,"E21")])]});var subQ2=makeQuery(id+"F2.imprint","INTERSECT",VERTEX,{"disambiguationData":[OD(0.0)],"derivedFrom":[subQ1,subQ0]});Q39=makeQuery(id+"F2.imprint","IMPRINT",FACE,{"disambiguationData":[TD([[makeQuery(id+"F2.imprint","IMPRINT",EDGE,{"disambiguationData":[TD([[subQ2,1.0]])],"derivedFrom":subQ0}),1.0]])]});}
            var Q40;
            {var subQ0=sQuery(id+"F2.wireOp",EDGE,"E23.17.0");var subQ1=makeQuery(id+"F1.opRevolve","SWEPT_EDGE",EDGE,{"disambiguationData":[OSD([sQuery(id+"F0.wireOp",EDGE,"E12"),sQuery(id+"F0.wireOp",EDGE,"E21")])]});var subQ2=makeQuery(id+"F2.imprint","INTERSECT",VERTEX,{"disambiguationData":[OD(0.0)],"derivedFrom":[subQ1,subQ0]});Q40=makeQuery(id+"F2.imprint","IMPRINT",FACE,{"disambiguationData":[TD([[makeQuery(id+"F2.imprint","IMPRINT",EDGE,{"disambiguationData":[TD([[subQ2,-1.0]])],"derivedFrom":subQ0}),1.0]])]});}
            var Q41;
            {var subQ0=sQuery(id+"F2.wireOp",EDGE,"E23.17.0");var subQ1=makeQuery(id+"F1.opRevolve","SWEPT_EDGE",EDGE,{"disambiguationData":[OSD([sQuery(id+"F0.wireOp",EDGE,"E12"),sQuery(id+"F0.wireOp",EDGE,"E21")])]});var subQ2=makeQuery(id+"F2.imprint","INTERSECT",VERTEX,{"disambiguationData":[OD(0.0)],"derivedFrom":[subQ1,subQ0]});Q41=makeQuery(id+"F2.imprint","IMPRINT",FACE,{"disambiguationData":[TD([[makeQuery(id+"F2.imprint","IMPRINT",EDGE,{"disambiguationData":[TD([[subQ2,1.0]])],"derivedFrom":subQ0}),1.0]])]});}
            var Q42;
            {var subQ0=sQuery(id+"F2.wireOp",EDGE,"E23.16.0");var subQ1=makeQuery(id+"F1.opRevolve","SWEPT_EDGE",EDGE,{"disambiguationData":[OSD([sQuery(id+"F0.wireOp",EDGE,"E12"),sQuery(id+"F0.wireOp",EDGE,"E21")])]});var subQ2=makeQuery(id+"F2.imprint","INTERSECT",VERTEX,{"disambiguationData":[OD(0.0)],"derivedFrom":[subQ1,subQ0]});Q42=makeQuery(id+"F2.imprint","IMPRINT",FACE,{"disambiguationData":[TD([[makeQuery(id+"F2.imprint","IMPRINT",EDGE,{"disambiguationData":[TD([[subQ2,-1.0]])],"derivedFrom":subQ0}),1.0]])]});}
            var Q43;
            {var subQ0=sQuery(id+"F2.wireOp",EDGE,"E23.16.0");var subQ1=makeQuery(id+"F1.opRevolve","SWEPT_EDGE",EDGE,{"disambiguationData":[OSD([sQuery(id+"F0.wireOp",EDGE,"E12"),sQuery(id+"F0.wireOp",EDGE,"E21")])]});var subQ2=makeQuery(id+"F2.imprint","INTERSECT",VERTEX,{"disambiguationData":[OD(0.0)],"derivedFrom":[subQ1,subQ0]});Q43=makeQuery(id+"F2.imprint","IMPRINT",FACE,{"disambiguationData":[TD([[makeQuery(id+"F2.imprint","IMPRINT",EDGE,{"disambiguationData":[TD([[subQ2,1.0]])],"derivedFrom":subQ0}),1.0]])]});}
            var Q44;
            {var subQ0=sQuery(id+"F2.wireOp",EDGE,"E23.20.0");var subQ1=makeQuery(id+"F1.opRevolve","SWEPT_EDGE",EDGE,{"disambiguationData":[OSD([sQuery(id+"F0.wireOp",EDGE,"E12"),sQuery(id+"F0.wireOp",EDGE,"E21")])]});var subQ2=makeQuery(id+"F2.imprint","INTERSECT",VERTEX,{"disambiguationData":[OD(0.0)],"derivedFrom":[subQ1,subQ0]});Q44=makeQuery(id+"F2.imprint","IMPRINT",FACE,{"disambiguationData":[TD([[makeQuery(id+"F2.imprint","IMPRINT",EDGE,{"disambiguationData":[TD([[subQ2,-1.0]])],"derivedFrom":subQ0}),1.0]])]});}
            var Q45;
            {var subQ0=sQuery(id+"F2.wireOp",EDGE,"E23.20.0");var subQ1=makeQuery(id+"F1.opRevolve","SWEPT_EDGE",EDGE,{"disambiguationData":[OSD([sQuery(id+"F0.wireOp",EDGE,"E12"),sQuery(id+"F0.wireOp",EDGE,"E21")])]});var subQ2=makeQuery(id+"F2.imprint","INTERSECT",VERTEX,{"disambiguationData":[OD(0.0)],"derivedFrom":[subQ1,subQ0]});Q45=makeQuery(id+"F2.imprint","IMPRINT",FACE,{"disambiguationData":[TD([[makeQuery(id+"F2.imprint","IMPRINT",EDGE,{"disambiguationData":[TD([[subQ2,1.0]])],"derivedFrom":subQ0}),1.0]])]});}
            var Q46;
            {var subQ0=sQuery(id+"F2.wireOp",EDGE,"E23.19.0");var subQ1=makeQuery(id+"F1.opRevolve","SWEPT_EDGE",EDGE,{"disambiguationData":[OSD([sQuery(id+"F0.wireOp",EDGE,"E12"),sQuery(id+"F0.wireOp",EDGE,"E21")])]});var subQ2=makeQuery(id+"F2.imprint","INTERSECT",VERTEX,{"disambiguationData":[OD(0.0)],"derivedFrom":[subQ1,subQ0]});Q46=makeQuery(id+"F2.imprint","IMPRINT",FACE,{"disambiguationData":[TD([[makeQuery(id+"F2.imprint","IMPRINT",EDGE,{"disambiguationData":[TD([[subQ2,-1.0]])],"derivedFrom":subQ0}),1.0]])]});}
            var Q47;
            {var subQ0=sQuery(id+"F2.wireOp",EDGE,"E23.19.0");var subQ1=makeQuery(id+"F1.opRevolve","SWEPT_EDGE",EDGE,{"disambiguationData":[OSD([sQuery(id+"F0.wireOp",EDGE,"E12"),sQuery(id+"F0.wireOp",EDGE,"E21")])]});var subQ2=makeQuery(id+"F2.imprint","INTERSECT",VERTEX,{"disambiguationData":[OD(0.0)],"derivedFrom":[subQ1,subQ0]});Q47=makeQuery(id+"F2.imprint","IMPRINT",FACE,{"disambiguationData":[TD([[makeQuery(id+"F2.imprint","IMPRINT",EDGE,{"disambiguationData":[TD([[subQ2,1.0]])],"derivedFrom":subQ0}),1.0]])]});}
            var Q48;
            {var subQ0=sQuery(id+"F2.wireOp",EDGE,"E23.18.0");var subQ1=makeQuery(id+"F1.opRevolve","SWEPT_EDGE",EDGE,{"disambiguationData":[OSD([sQuery(id+"F0.wireOp",EDGE,"E12"),sQuery(id+"F0.wireOp",EDGE,"E21")])]});var subQ2=makeQuery(id+"F2.imprint","INTERSECT",VERTEX,{"disambiguationData":[OD(0.0)],"derivedFrom":[subQ1,subQ0]});Q48=makeQuery(id+"F2.imprint","IMPRINT",FACE,{"disambiguationData":[TD([[makeQuery(id+"F2.imprint","IMPRINT",EDGE,{"disambiguationData":[TD([[subQ2,-1.0]])],"derivedFrom":subQ0}),1.0]])]});}
            var Q49;
            {var subQ0=sQuery(id+"F2.wireOp",EDGE,"E23.18.0");var subQ1=makeQuery(id+"F1.opRevolve","SWEPT_EDGE",EDGE,{"disambiguationData":[OSD([sQuery(id+"F0.wireOp",EDGE,"E12"),sQuery(id+"F0.wireOp",EDGE,"E21")])]});var subQ2=makeQuery(id+"F2.imprint","INTERSECT",VERTEX,{"disambiguationData":[OD(0.0)],"derivedFrom":[subQ1,subQ0]});Q49=makeQuery(id+"F2.imprint","IMPRINT",FACE,{"disambiguationData":[TD([[makeQuery(id+"F2.imprint","IMPRINT",EDGE,{"disambiguationData":[TD([[subQ2,1.0]])],"derivedFrom":subQ0}),1.0]])]});}
            var Q50;
            {var subQ0=sQuery(id+"F2.wireOp",EDGE,"E23.23.0");var subQ1=makeQuery(id+"F1.opRevolve","SWEPT_EDGE",EDGE,{"disambiguationData":[OSD([sQuery(id+"F0.wireOp",EDGE,"E12"),sQuery(id+"F0.wireOp",EDGE,"E21")])]});var subQ2=makeQuery(id+"F2.imprint","INTERSECT",VERTEX,{"disambiguationData":[OD(0.0)],"derivedFrom":[subQ1,subQ0]});Q50=makeQuery(id+"F2.imprint","IMPRINT",FACE,{"disambiguationData":[TD([[makeQuery(id+"F2.imprint","IMPRINT",EDGE,{"disambiguationData":[TD([[subQ2,-1.0]])],"derivedFrom":subQ0}),1.0]])]});}
            var Q51;
            {var subQ0=sQuery(id+"F2.wireOp",EDGE,"E23.23.0");var subQ1=makeQuery(id+"F1.opRevolve","SWEPT_EDGE",EDGE,{"disambiguationData":[OSD([sQuery(id+"F0.wireOp",EDGE,"E12"),sQuery(id+"F0.wireOp",EDGE,"E21")])]});var subQ2=makeQuery(id+"F2.imprint","INTERSECT",VERTEX,{"disambiguationData":[OD(0.0)],"derivedFrom":[subQ1,subQ0]});Q51=makeQuery(id+"F2.imprint","IMPRINT",FACE,{"disambiguationData":[TD([[makeQuery(id+"F2.imprint","IMPRINT",EDGE,{"disambiguationData":[TD([[subQ2,1.0]])],"derivedFrom":subQ0}),1.0]])]});}
            var Q52;
            {var subQ0=sQuery(id+"F2.wireOp",EDGE,"E23.22.0");var subQ1=makeQuery(id+"F1.opRevolve","SWEPT_EDGE",EDGE,{"disambiguationData":[OSD([sQuery(id+"F0.wireOp",EDGE,"E12"),sQuery(id+"F0.wireOp",EDGE,"E21")])]});var subQ2=makeQuery(id+"F2.imprint","INTERSECT",VERTEX,{"disambiguationData":[OD(0.0)],"derivedFrom":[subQ1,subQ0]});Q52=makeQuery(id+"F2.imprint","IMPRINT",FACE,{"disambiguationData":[TD([[makeQuery(id+"F2.imprint","IMPRINT",EDGE,{"disambiguationData":[TD([[subQ2,-1.0]])],"derivedFrom":subQ0}),1.0]])]});}
            var Q53;
            {var subQ0=sQuery(id+"F2.wireOp",EDGE,"E23.22.0");var subQ1=makeQuery(id+"F1.opRevolve","SWEPT_EDGE",EDGE,{"disambiguationData":[OSD([sQuery(id+"F0.wireOp",EDGE,"E12"),sQuery(id+"F0.wireOp",EDGE,"E21")])]});var subQ2=makeQuery(id+"F2.imprint","INTERSECT",VERTEX,{"disambiguationData":[OD(0.0)],"derivedFrom":[subQ1,subQ0]});Q53=makeQuery(id+"F2.imprint","IMPRINT",FACE,{"disambiguationData":[TD([[makeQuery(id+"F2.imprint","IMPRINT",EDGE,{"disambiguationData":[TD([[subQ2,1.0]])],"derivedFrom":subQ0}),1.0]])]});}
            var Q54;
            {var subQ0=sQuery(id+"F2.wireOp",EDGE,"E23.21.0");var subQ1=makeQuery(id+"F1.opRevolve","SWEPT_EDGE",EDGE,{"disambiguationData":[OSD([sQuery(id+"F0.wireOp",EDGE,"E12"),sQuery(id+"F0.wireOp",EDGE,"E21")])]});var subQ2=makeQuery(id+"F2.imprint","INTERSECT",VERTEX,{"disambiguationData":[OD(0.0)],"derivedFrom":[subQ1,subQ0]});Q54=makeQuery(id+"F2.imprint","IMPRINT",FACE,{"disambiguationData":[TD([[makeQuery(id+"F2.imprint","IMPRINT",EDGE,{"disambiguationData":[TD([[subQ2,-1.0]])],"derivedFrom":subQ0}),1.0]])]});}
            var Q55;
            {var subQ0=sQuery(id+"F2.wireOp",EDGE,"E23.21.0");var subQ1=makeQuery(id+"F1.opRevolve","SWEPT_EDGE",EDGE,{"disambiguationData":[OSD([sQuery(id+"F0.wireOp",EDGE,"E12"),sQuery(id+"F0.wireOp",EDGE,"E21")])]});var subQ2=makeQuery(id+"F2.imprint","INTERSECT",VERTEX,{"disambiguationData":[OD(0.0)],"derivedFrom":[subQ1,subQ0]});Q55=makeQuery(id+"F2.imprint","IMPRINT",FACE,{"disambiguationData":[TD([[makeQuery(id+"F2.imprint","IMPRINT",EDGE,{"disambiguationData":[TD([[subQ2,1.0]])],"derivedFrom":subQ0}),1.0]])]});}
            var Q56;
            {var subQ0=sQuery(id+"F2.wireOp",EDGE,"E23.24.0");var subQ1=makeQuery(id+"F1.opRevolve","SWEPT_EDGE",EDGE,{"disambiguationData":[OSD([sQuery(id+"F0.wireOp",EDGE,"E12"),sQuery(id+"F0.wireOp",EDGE,"E21")])]});var subQ2=makeQuery(id+"F2.imprint","INTERSECT",VERTEX,{"disambiguationData":[OD(0.0)],"derivedFrom":[subQ1,subQ0]});Q56=makeQuery(id+"F2.imprint","IMPRINT",FACE,{"disambiguationData":[TD([[makeQuery(id+"F2.imprint","IMPRINT",EDGE,{"disambiguationData":[TD([[subQ2,1.0]])],"derivedFrom":subQ0}),1.0]])]});}
            var Q57;
            {var subQ0=sQuery(id+"F2.wireOp",EDGE,"E23.24.0");var subQ1=makeQuery(id+"F1.opRevolve","SWEPT_EDGE",EDGE,{"disambiguationData":[OSD([sQuery(id+"F0.wireOp",EDGE,"E12"),sQuery(id+"F0.wireOp",EDGE,"E21")])]});var subQ2=makeQuery(id+"F2.imprint","INTERSECT",VERTEX,{"disambiguationData":[OD(0.0)],"derivedFrom":[subQ1,subQ0]});Q57=makeQuery(id+"F2.imprint","IMPRINT",FACE,{"disambiguationData":[TD([[makeQuery(id+"F2.imprint","IMPRINT",EDGE,{"disambiguationData":[TD([[subQ2,-1.0]])],"derivedFrom":subQ0}),1.0]])]});}
            var Q58;
            {var subQ0=sQuery(id+"F2.wireOp",EDGE,"E23.25.0");var subQ1=makeQuery(id+"F1.opRevolve","SWEPT_EDGE",EDGE,{"disambiguationData":[OSD([sQuery(id+"F0.wireOp",EDGE,"E12"),sQuery(id+"F0.wireOp",EDGE,"E21")])]});var subQ2=makeQuery(id+"F2.imprint","INTERSECT",VERTEX,{"disambiguationData":[OD(0.0)],"derivedFrom":[subQ1,subQ0]});Q58=makeQuery(id+"F2.imprint","IMPRINT",FACE,{"disambiguationData":[TD([[makeQuery(id+"F2.imprint","IMPRINT",EDGE,{"disambiguationData":[TD([[subQ2,-1.0]])],"derivedFrom":subQ0}),1.0]])]});}
            var Q59;
            {var subQ0=sQuery(id+"F2.wireOp",EDGE,"E23.25.0");var subQ1=makeQuery(id+"F1.opRevolve","SWEPT_EDGE",EDGE,{"disambiguationData":[OSD([sQuery(id+"F0.wireOp",EDGE,"E12"),sQuery(id+"F0.wireOp",EDGE,"E21")])]});var subQ2=makeQuery(id+"F2.imprint","INTERSECT",VERTEX,{"disambiguationData":[OD(0.0)],"derivedFrom":[subQ1,subQ0]});Q59=makeQuery(id+"F2.imprint","IMPRINT",FACE,{"disambiguationData":[TD([[makeQuery(id+"F2.imprint","IMPRINT",EDGE,{"disambiguationData":[TD([[subQ2,1.0]])],"derivedFrom":subQ0}),1.0]])]});}
            var Q60;
            {var subQ0=sQuery(id+"F2.wireOp",EDGE,"E23.26.0");var subQ1=makeQuery(id+"F1.opRevolve","SWEPT_EDGE",EDGE,{"disambiguationData":[OSD([sQuery(id+"F0.wireOp",EDGE,"E12"),sQuery(id+"F0.wireOp",EDGE,"E21")])]});var subQ2=makeQuery(id+"F2.imprint","INTERSECT",VERTEX,{"disambiguationData":[OD(0.0)],"derivedFrom":[subQ1,subQ0]});Q60=makeQuery(id+"F2.imprint","IMPRINT",FACE,{"disambiguationData":[TD([[makeQuery(id+"F2.imprint","IMPRINT",EDGE,{"disambiguationData":[TD([[subQ2,1.0]])],"derivedFrom":subQ0}),1.0]])]});}
            var Q61;
            {var subQ0=sQuery(id+"F2.wireOp",EDGE,"E23.26.0");var subQ1=makeQuery(id+"F1.opRevolve","SWEPT_EDGE",EDGE,{"disambiguationData":[OSD([sQuery(id+"F0.wireOp",EDGE,"E12"),sQuery(id+"F0.wireOp",EDGE,"E21")])]});var subQ2=makeQuery(id+"F2.imprint","INTERSECT",VERTEX,{"disambiguationData":[OD(0.0)],"derivedFrom":[subQ1,subQ0]});Q61=makeQuery(id+"F2.imprint","IMPRINT",FACE,{"disambiguationData":[TD([[makeQuery(id+"F2.imprint","IMPRINT",EDGE,{"disambiguationData":[TD([[subQ2,-1.0]])],"derivedFrom":subQ0}),1.0]])]});}
            var Q62;
            {var subQ0=sQuery(id+"F2.wireOp",EDGE,"E23.27.0");var subQ1=makeQuery(id+"F1.opRevolve","SWEPT_EDGE",EDGE,{"disambiguationData":[OSD([sQuery(id+"F0.wireOp",EDGE,"E12"),sQuery(id+"F0.wireOp",EDGE,"E21")])]});var subQ2=makeQuery(id+"F2.imprint","INTERSECT",VERTEX,{"disambiguationData":[OD(0.0)],"derivedFrom":[subQ1,subQ0]});Q62=makeQuery(id+"F2.imprint","IMPRINT",FACE,{"disambiguationData":[TD([[makeQuery(id+"F2.imprint","IMPRINT",EDGE,{"disambiguationData":[TD([[subQ2,-1.0]])],"derivedFrom":subQ0}),1.0]])]});}
            var Q63;
            {var subQ0=sQuery(id+"F2.wireOp",EDGE,"E23.27.0");var subQ1=makeQuery(id+"F1.opRevolve","SWEPT_EDGE",EDGE,{"disambiguationData":[OSD([sQuery(id+"F0.wireOp",EDGE,"E12"),sQuery(id+"F0.wireOp",EDGE,"E21")])]});var subQ2=makeQuery(id+"F2.imprint","INTERSECT",VERTEX,{"disambiguationData":[OD(0.0)],"derivedFrom":[subQ1,subQ0]});Q63=makeQuery(id+"F2.imprint","IMPRINT",FACE,{"disambiguationData":[TD([[makeQuery(id+"F2.imprint","IMPRINT",EDGE,{"disambiguationData":[TD([[subQ2,1.0]])],"derivedFrom":subQ0}),1.0]])]});}
            var Q64;
            {var subQ0=sQuery(id+"F2.wireOp",EDGE,"E23.28.0");var subQ1=makeQuery(id+"F1.opRevolve","SWEPT_EDGE",EDGE,{"disambiguationData":[OSD([sQuery(id+"F0.wireOp",EDGE,"E12"),sQuery(id+"F0.wireOp",EDGE,"E21")])]});var subQ2=makeQuery(id+"F2.imprint","INTERSECT",VERTEX,{"disambiguationData":[OD(0.0)],"derivedFrom":[subQ1,subQ0]});Q64=makeQuery(id+"F2.imprint","IMPRINT",FACE,{"disambiguationData":[TD([[makeQuery(id+"F2.imprint","IMPRINT",EDGE,{"disambiguationData":[TD([[subQ2,-1.0]])],"derivedFrom":subQ0}),1.0]])]});}
            var Q65;
            {var subQ0=sQuery(id+"F2.wireOp",EDGE,"E23.28.0");var subQ1=makeQuery(id+"F1.opRevolve","SWEPT_EDGE",EDGE,{"disambiguationData":[OSD([sQuery(id+"F0.wireOp",EDGE,"E12"),sQuery(id+"F0.wireOp",EDGE,"E21")])]});var subQ2=makeQuery(id+"F2.imprint","INTERSECT",VERTEX,{"disambiguationData":[OD(0.0)],"derivedFrom":[subQ1,subQ0]});Q65=makeQuery(id+"F2.imprint","IMPRINT",FACE,{"disambiguationData":[TD([[makeQuery(id+"F2.imprint","IMPRINT",EDGE,{"disambiguationData":[TD([[subQ2,1.0]])],"derivedFrom":subQ0}),1.0]])]});}
            var Q66;
            {var subQ0=sQuery(id+"F2.wireOp",EDGE,"E23.29.0");var subQ1=makeQuery(id+"F1.opRevolve","SWEPT_EDGE",EDGE,{"disambiguationData":[OSD([sQuery(id+"F0.wireOp",EDGE,"E12"),sQuery(id+"F0.wireOp",EDGE,"E21")])]});var subQ2=makeQuery(id+"F2.imprint","INTERSECT",VERTEX,{"disambiguationData":[OD(0.0)],"derivedFrom":[subQ1,subQ0]});Q66=makeQuery(id+"F2.imprint","IMPRINT",FACE,{"disambiguationData":[TD([[makeQuery(id+"F2.imprint","IMPRINT",EDGE,{"disambiguationData":[TD([[subQ2,1.0]])],"derivedFrom":subQ0}),1.0]])]});}
            var Q67;
            {var subQ0=sQuery(id+"F2.wireOp",EDGE,"E23.29.0");var subQ1=makeQuery(id+"F1.opRevolve","SWEPT_EDGE",EDGE,{"disambiguationData":[OSD([sQuery(id+"F0.wireOp",EDGE,"E12"),sQuery(id+"F0.wireOp",EDGE,"E21")])]});var subQ2=makeQuery(id+"F2.imprint","INTERSECT",VERTEX,{"disambiguationData":[OD(0.0)],"derivedFrom":[subQ1,subQ0]});Q67=makeQuery(id+"F2.imprint","IMPRINT",FACE,{"disambiguationData":[TD([[makeQuery(id+"F2.imprint","IMPRINT",EDGE,{"disambiguationData":[TD([[subQ2,-1.0]])],"derivedFrom":subQ0}),1.0]])]});}
            var Q68;
            {var subQ0=sQuery(id+"F2.wireOp",EDGE,"E23.30.0");var subQ1=makeQuery(id+"F1.opRevolve","SWEPT_EDGE",EDGE,{"disambiguationData":[OSD([sQuery(id+"F0.wireOp",EDGE,"E12"),sQuery(id+"F0.wireOp",EDGE,"E21")])]});var subQ2=makeQuery(id+"F2.imprint","INTERSECT",VERTEX,{"disambiguationData":[OD(0.0)],"derivedFrom":[subQ1,subQ0]});Q68=makeQuery(id+"F2.imprint","IMPRINT",FACE,{"disambiguationData":[TD([[makeQuery(id+"F2.imprint","IMPRINT",EDGE,{"disambiguationData":[TD([[subQ2,1.0]])],"derivedFrom":subQ0}),1.0]])]});}
            var Q69;
            {var subQ0=sQuery(id+"F2.wireOp",EDGE,"E23.30.0");var subQ1=makeQuery(id+"F1.opRevolve","SWEPT_EDGE",EDGE,{"disambiguationData":[OSD([sQuery(id+"F0.wireOp",EDGE,"E12"),sQuery(id+"F0.wireOp",EDGE,"E21")])]});var subQ2=makeQuery(id+"F2.imprint","INTERSECT",VERTEX,{"disambiguationData":[OD(0.0)],"derivedFrom":[subQ1,subQ0]});Q69=makeQuery(id+"F2.imprint","IMPRINT",FACE,{"disambiguationData":[TD([[makeQuery(id+"F2.imprint","IMPRINT",EDGE,{"disambiguationData":[TD([[subQ2,-1.0]])],"derivedFrom":subQ0}),1.0]])]});}
            var Q70;
            {var subQ0=sQuery(id+"F2.wireOp",EDGE,"E23.31.0");var subQ1=makeQuery(id+"F1.opRevolve","SWEPT_EDGE",EDGE,{"disambiguationData":[OSD([sQuery(id+"F0.wireOp",EDGE,"E12"),sQuery(id+"F0.wireOp",EDGE,"E21")])]});var subQ2=makeQuery(id+"F2.imprint","INTERSECT",VERTEX,{"disambiguationData":[OD(0.0)],"derivedFrom":[subQ1,subQ0]});Q70=makeQuery(id+"F2.imprint","IMPRINT",FACE,{"disambiguationData":[TD([[makeQuery(id+"F2.imprint","IMPRINT",EDGE,{"disambiguationData":[TD([[subQ2,1.0]])],"derivedFrom":subQ0}),1.0]])]});}
            var Q71;
            {var subQ0=sQuery(id+"F2.wireOp",EDGE,"E23.31.0");var subQ1=makeQuery(id+"F1.opRevolve","SWEPT_EDGE",EDGE,{"disambiguationData":[OSD([sQuery(id+"F0.wireOp",EDGE,"E12"),sQuery(id+"F0.wireOp",EDGE,"E21")])]});var subQ2=makeQuery(id+"F2.imprint","INTERSECT",VERTEX,{"disambiguationData":[OD(0.0)],"derivedFrom":[subQ1,subQ0]});Q71=makeQuery(id+"F2.imprint","IMPRINT",FACE,{"disambiguationData":[TD([[makeQuery(id+"F2.imprint","IMPRINT",EDGE,{"disambiguationData":[TD([[subQ2,-1.0]])],"derivedFrom":subQ0}),1.0]])]});}
            var Q72;
            {var subQ0=sQuery(id+"F2.wireOp",EDGE,"E23.32.0");var subQ1=makeQuery(id+"F1.opRevolve","SWEPT_EDGE",EDGE,{"disambiguationData":[OSD([sQuery(id+"F0.wireOp",EDGE,"E12"),sQuery(id+"F0.wireOp",EDGE,"E21")])]});var subQ2=makeQuery(id+"F2.imprint","INTERSECT",VERTEX,{"disambiguationData":[OD(0.0)],"derivedFrom":[subQ1,subQ0]});Q72=makeQuery(id+"F2.imprint","IMPRINT",FACE,{"disambiguationData":[TD([[makeQuery(id+"F2.imprint","IMPRINT",EDGE,{"disambiguationData":[TD([[subQ2,1.0]])],"derivedFrom":subQ0}),1.0]])]});}
            var Q73;
            {var subQ0=sQuery(id+"F2.wireOp",EDGE,"E23.32.0");var subQ1=makeQuery(id+"F1.opRevolve","SWEPT_EDGE",EDGE,{"disambiguationData":[OSD([sQuery(id+"F0.wireOp",EDGE,"E12"),sQuery(id+"F0.wireOp",EDGE,"E21")])]});var subQ2=makeQuery(id+"F2.imprint","INTERSECT",VERTEX,{"disambiguationData":[OD(0.0)],"derivedFrom":[subQ1,subQ0]});Q73=makeQuery(id+"F2.imprint","IMPRINT",FACE,{"disambiguationData":[TD([[makeQuery(id+"F2.imprint","IMPRINT",EDGE,{"disambiguationData":[TD([[subQ2,-1.0]])],"derivedFrom":subQ0}),1.0]])]});}
            var Q74;
            {var subQ0=sQuery(id+"F2.wireOp",EDGE,"E23.33.0");var subQ1=makeQuery(id+"F1.opRevolve","SWEPT_EDGE",EDGE,{"disambiguationData":[OSD([sQuery(id+"F0.wireOp",EDGE,"E12"),sQuery(id+"F0.wireOp",EDGE,"E21")])]});var subQ2=makeQuery(id+"F2.imprint","INTERSECT",VERTEX,{"disambiguationData":[OD(0.0)],"derivedFrom":[subQ1,subQ0]});Q74=makeQuery(id+"F2.imprint","IMPRINT",FACE,{"disambiguationData":[TD([[makeQuery(id+"F2.imprint","IMPRINT",EDGE,{"disambiguationData":[TD([[subQ2,1.0]])],"derivedFrom":subQ0}),1.0]])]});}
            var Q75;
            {var subQ0=sQuery(id+"F2.wireOp",EDGE,"E23.33.0");var subQ1=makeQuery(id+"F1.opRevolve","SWEPT_EDGE",EDGE,{"disambiguationData":[OSD([sQuery(id+"F0.wireOp",EDGE,"E12"),sQuery(id+"F0.wireOp",EDGE,"E21")])]});var subQ2=makeQuery(id+"F2.imprint","INTERSECT",VERTEX,{"disambiguationData":[OD(0.0)],"derivedFrom":[subQ1,subQ0]});Q75=makeQuery(id+"F2.imprint","IMPRINT",FACE,{"disambiguationData":[TD([[makeQuery(id+"F2.imprint","IMPRINT",EDGE,{"disambiguationData":[TD([[subQ2,-1.0]])],"derivedFrom":subQ0}),1.0]])]});}
            var Q76;
            {var subQ0=sQuery(id+"F2.wireOp",EDGE,"E23.34.0");var subQ1=makeQuery(id+"F1.opRevolve","SWEPT_EDGE",EDGE,{"disambiguationData":[OSD([sQuery(id+"F0.wireOp",EDGE,"E12"),sQuery(id+"F0.wireOp",EDGE,"E21")])]});var subQ2=makeQuery(id+"F2.imprint","INTERSECT",VERTEX,{"disambiguationData":[OD(0.0)],"derivedFrom":[subQ1,subQ0]});Q76=makeQuery(id+"F2.imprint","IMPRINT",FACE,{"disambiguationData":[TD([[makeQuery(id+"F2.imprint","IMPRINT",EDGE,{"disambiguationData":[TD([[subQ2,-1.0]])],"derivedFrom":subQ0}),1.0]])]});}
            var Q77;
            {var subQ0=sQuery(id+"F2.wireOp",EDGE,"E23.34.0");var subQ1=makeQuery(id+"F1.opRevolve","SWEPT_EDGE",EDGE,{"disambiguationData":[OSD([sQuery(id+"F0.wireOp",EDGE,"E12"),sQuery(id+"F0.wireOp",EDGE,"E21")])]});var subQ2=makeQuery(id+"F2.imprint","INTERSECT",VERTEX,{"disambiguationData":[OD(0.0)],"derivedFrom":[subQ1,subQ0]});Q77=makeQuery(id+"F2.imprint","IMPRINT",FACE,{"disambiguationData":[TD([[makeQuery(id+"F2.imprint","IMPRINT",EDGE,{"disambiguationData":[TD([[subQ2,1.0]])],"derivedFrom":subQ0}),1.0]])]});}
            var Q78;
            {var subQ0=sQuery(id+"F2.wireOp",EDGE,"E23.45.0");var subQ1=makeQuery(id+"F1.opRevolve","SWEPT_EDGE",EDGE,{"disambiguationData":[OSD([sQuery(id+"F0.wireOp",EDGE,"E12"),sQuery(id+"F0.wireOp",EDGE,"E21")])]});var subQ2=makeQuery(id+"F2.imprint","INTERSECT",VERTEX,{"disambiguationData":[OD(0.0)],"derivedFrom":[subQ1,subQ0]});Q78=makeQuery(id+"F2.imprint","IMPRINT",FACE,{"disambiguationData":[TD([[makeQuery(id+"F2.imprint","IMPRINT",EDGE,{"disambiguationData":[TD([[subQ2,1.0]])],"derivedFrom":subQ0}),1.0]])]});}
            var Q79;
            {var subQ0=sQuery(id+"F2.wireOp",EDGE,"E23.45.0");var subQ1=makeQuery(id+"F1.opRevolve","SWEPT_EDGE",EDGE,{"disambiguationData":[OSD([sQuery(id+"F0.wireOp",EDGE,"E12"),sQuery(id+"F0.wireOp",EDGE,"E21")])]});var subQ2=makeQuery(id+"F2.imprint","INTERSECT",VERTEX,{"disambiguationData":[OD(0.0)],"derivedFrom":[subQ1,subQ0]});Q79=makeQuery(id+"F2.imprint","IMPRINT",FACE,{"disambiguationData":[TD([[makeQuery(id+"F2.imprint","IMPRINT",EDGE,{"disambiguationData":[TD([[subQ2,-1.0]])],"derivedFrom":subQ0}),1.0]])]});}
            var Q80;
            {var subQ0=sQuery(id+"F2.wireOp",EDGE,"E23.44.0");var subQ1=makeQuery(id+"F1.opRevolve","SWEPT_EDGE",EDGE,{"disambiguationData":[OSD([sQuery(id+"F0.wireOp",EDGE,"E12"),sQuery(id+"F0.wireOp",EDGE,"E21")])]});var subQ2=makeQuery(id+"F2.imprint","INTERSECT",VERTEX,{"disambiguationData":[OD(0.0)],"derivedFrom":[subQ1,subQ0]});Q80=makeQuery(id+"F2.imprint","IMPRINT",FACE,{"disambiguationData":[TD([[makeQuery(id+"F2.imprint","IMPRINT",EDGE,{"disambiguationData":[TD([[subQ2,1.0]])],"derivedFrom":subQ0}),1.0]])]});}
            var Q81;
            {var subQ0=sQuery(id+"F2.wireOp",EDGE,"E23.44.0");var subQ1=makeQuery(id+"F1.opRevolve","SWEPT_EDGE",EDGE,{"disambiguationData":[OSD([sQuery(id+"F0.wireOp",EDGE,"E12"),sQuery(id+"F0.wireOp",EDGE,"E21")])]});var subQ2=makeQuery(id+"F2.imprint","INTERSECT",VERTEX,{"disambiguationData":[OD(0.0)],"derivedFrom":[subQ1,subQ0]});Q81=makeQuery(id+"F2.imprint","IMPRINT",FACE,{"disambiguationData":[TD([[makeQuery(id+"F2.imprint","IMPRINT",EDGE,{"disambiguationData":[TD([[subQ2,-1.0]])],"derivedFrom":subQ0}),1.0]])]});}
            var Q82;
            {var subQ0=sQuery(id+"F2.wireOp",EDGE,"E23.41.0");var subQ1=makeQuery(id+"F1.opRevolve","SWEPT_EDGE",EDGE,{"disambiguationData":[OSD([sQuery(id+"F0.wireOp",EDGE,"E12"),sQuery(id+"F0.wireOp",EDGE,"E21")])]});var subQ2=makeQuery(id+"F2.imprint","INTERSECT",VERTEX,{"disambiguationData":[OD(0.0)],"derivedFrom":[subQ1,subQ0]});Q82=makeQuery(id+"F2.imprint","IMPRINT",FACE,{"disambiguationData":[TD([[makeQuery(id+"F2.imprint","IMPRINT",EDGE,{"disambiguationData":[TD([[subQ2,-1.0]])],"derivedFrom":subQ0}),1.0]])]});}
            var Q83;
            {var subQ0=sQuery(id+"F2.wireOp",EDGE,"E23.41.0");var subQ1=makeQuery(id+"F1.opRevolve","SWEPT_EDGE",EDGE,{"disambiguationData":[OSD([sQuery(id+"F0.wireOp",EDGE,"E12"),sQuery(id+"F0.wireOp",EDGE,"E21")])]});var subQ2=makeQuery(id+"F2.imprint","INTERSECT",VERTEX,{"disambiguationData":[OD(0.0)],"derivedFrom":[subQ1,subQ0]});Q83=makeQuery(id+"F2.imprint","IMPRINT",FACE,{"disambiguationData":[TD([[makeQuery(id+"F2.imprint","IMPRINT",EDGE,{"disambiguationData":[TD([[subQ2,1.0]])],"derivedFrom":subQ0}),1.0]])]});}
            var Q84;
            {var subQ0=sQuery(id+"F2.wireOp",EDGE,"E23.42.0");var subQ1=makeQuery(id+"F1.opRevolve","SWEPT_EDGE",EDGE,{"disambiguationData":[OSD([sQuery(id+"F0.wireOp",EDGE,"E12"),sQuery(id+"F0.wireOp",EDGE,"E21")])]});var subQ2=makeQuery(id+"F2.imprint","INTERSECT",VERTEX,{"disambiguationData":[OD(0.0)],"derivedFrom":[subQ1,subQ0]});Q84=makeQuery(id+"F2.imprint","IMPRINT",FACE,{"disambiguationData":[TD([[makeQuery(id+"F2.imprint","IMPRINT",EDGE,{"disambiguationData":[TD([[subQ2,-1.0]])],"derivedFrom":subQ0}),1.0]])]});}
            var Q85;
            {var subQ0=sQuery(id+"F2.wireOp",EDGE,"E23.42.0");var subQ1=makeQuery(id+"F1.opRevolve","SWEPT_EDGE",EDGE,{"disambiguationData":[OSD([sQuery(id+"F0.wireOp",EDGE,"E12"),sQuery(id+"F0.wireOp",EDGE,"E21")])]});var subQ2=makeQuery(id+"F2.imprint","INTERSECT",VERTEX,{"disambiguationData":[OD(0.0)],"derivedFrom":[subQ1,subQ0]});Q85=makeQuery(id+"F2.imprint","IMPRINT",FACE,{"disambiguationData":[TD([[makeQuery(id+"F2.imprint","IMPRINT",EDGE,{"disambiguationData":[TD([[subQ2,1.0]])],"derivedFrom":subQ0}),1.0]])]});}
            var Q86;
            {var subQ0=sQuery(id+"F2.wireOp",EDGE,"E23.43.0");var subQ1=makeQuery(id+"F1.opRevolve","SWEPT_EDGE",EDGE,{"disambiguationData":[OSD([sQuery(id+"F0.wireOp",EDGE,"E12"),sQuery(id+"F0.wireOp",EDGE,"E21")])]});var subQ2=makeQuery(id+"F2.imprint","INTERSECT",VERTEX,{"disambiguationData":[OD(0.0)],"derivedFrom":[subQ1,subQ0]});Q86=makeQuery(id+"F2.imprint","IMPRINT",FACE,{"disambiguationData":[TD([[makeQuery(id+"F2.imprint","IMPRINT",EDGE,{"disambiguationData":[TD([[subQ2,-1.0]])],"derivedFrom":subQ0}),1.0]])]});}
            var Q87;
            {var subQ0=sQuery(id+"F2.wireOp",EDGE,"E23.43.0");var subQ1=makeQuery(id+"F1.opRevolve","SWEPT_EDGE",EDGE,{"disambiguationData":[OSD([sQuery(id+"F0.wireOp",EDGE,"E12"),sQuery(id+"F0.wireOp",EDGE,"E21")])]});var subQ2=makeQuery(id+"F2.imprint","INTERSECT",VERTEX,{"disambiguationData":[OD(0.0)],"derivedFrom":[subQ1,subQ0]});Q87=makeQuery(id+"F2.imprint","IMPRINT",FACE,{"disambiguationData":[TD([[makeQuery(id+"F2.imprint","IMPRINT",EDGE,{"disambiguationData":[TD([[subQ2,1.0]])],"derivedFrom":subQ0}),1.0]])]});}
            var Q88;
            {var subQ0=sQuery(id+"F2.wireOp",EDGE,"E23.40.0");var subQ1=makeQuery(id+"F1.opRevolve","SWEPT_EDGE",EDGE,{"disambiguationData":[OSD([sQuery(id+"F0.wireOp",EDGE,"E12"),sQuery(id+"F0.wireOp",EDGE,"E21")])]});var subQ2=makeQuery(id+"F2.imprint","INTERSECT",VERTEX,{"disambiguationData":[OD(0.0)],"derivedFrom":[subQ1,subQ0]});Q88=makeQuery(id+"F2.imprint","IMPRINT",FACE,{"disambiguationData":[TD([[makeQuery(id+"F2.imprint","IMPRINT",EDGE,{"disambiguationData":[TD([[subQ2,1.0]])],"derivedFrom":subQ0}),1.0]])]});}
            var Q89;
            {var subQ0=sQuery(id+"F2.wireOp",EDGE,"E23.40.0");var subQ1=makeQuery(id+"F1.opRevolve","SWEPT_EDGE",EDGE,{"disambiguationData":[OSD([sQuery(id+"F0.wireOp",EDGE,"E12"),sQuery(id+"F0.wireOp",EDGE,"E21")])]});var subQ2=makeQuery(id+"F2.imprint","INTERSECT",VERTEX,{"disambiguationData":[OD(0.0)],"derivedFrom":[subQ1,subQ0]});Q89=makeQuery(id+"F2.imprint","IMPRINT",FACE,{"disambiguationData":[TD([[makeQuery(id+"F2.imprint","IMPRINT",EDGE,{"disambiguationData":[TD([[subQ2,-1.0]])],"derivedFrom":subQ0}),1.0]])]});}
            var Q90;
            {var subQ0=sQuery(id+"F2.wireOp",EDGE,"E23.39.0");var subQ1=makeQuery(id+"F1.opRevolve","SWEPT_EDGE",EDGE,{"disambiguationData":[OSD([sQuery(id+"F0.wireOp",EDGE,"E12"),sQuery(id+"F0.wireOp",EDGE,"E21")])]});var subQ2=makeQuery(id+"F2.imprint","INTERSECT",VERTEX,{"disambiguationData":[OD(0.0)],"derivedFrom":[subQ1,subQ0]});Q90=makeQuery(id+"F2.imprint","IMPRINT",FACE,{"disambiguationData":[TD([[makeQuery(id+"F2.imprint","IMPRINT",EDGE,{"disambiguationData":[TD([[subQ2,1.0]])],"derivedFrom":subQ0}),1.0]])]});}
            var Q91;
            {var subQ0=sQuery(id+"F2.wireOp",EDGE,"E23.39.0");var subQ1=makeQuery(id+"F1.opRevolve","SWEPT_EDGE",EDGE,{"disambiguationData":[OSD([sQuery(id+"F0.wireOp",EDGE,"E12"),sQuery(id+"F0.wireOp",EDGE,"E21")])]});var subQ2=makeQuery(id+"F2.imprint","INTERSECT",VERTEX,{"disambiguationData":[OD(0.0)],"derivedFrom":[subQ1,subQ0]});Q91=makeQuery(id+"F2.imprint","IMPRINT",FACE,{"disambiguationData":[TD([[makeQuery(id+"F2.imprint","IMPRINT",EDGE,{"disambiguationData":[TD([[subQ2,-1.0]])],"derivedFrom":subQ0}),1.0]])]});}
            var Q92;
            {var subQ0=sQuery(id+"F2.wireOp",EDGE,"E23.35.0");var subQ1=makeQuery(id+"F1.opRevolve","SWEPT_EDGE",EDGE,{"disambiguationData":[OSD([sQuery(id+"F0.wireOp",EDGE,"E12"),sQuery(id+"F0.wireOp",EDGE,"E21")])]});var subQ2=makeQuery(id+"F2.imprint","INTERSECT",VERTEX,{"disambiguationData":[OD(0.0)],"derivedFrom":[subQ1,subQ0]});Q92=makeQuery(id+"F2.imprint","IMPRINT",FACE,{"disambiguationData":[TD([[makeQuery(id+"F2.imprint","IMPRINT",EDGE,{"disambiguationData":[TD([[subQ2,1.0]])],"derivedFrom":subQ0}),1.0]])]});}
            var Q93;
            {var subQ0=sQuery(id+"F2.wireOp",EDGE,"E23.35.0");var subQ1=makeQuery(id+"F1.opRevolve","SWEPT_EDGE",EDGE,{"disambiguationData":[OSD([sQuery(id+"F0.wireOp",EDGE,"E12"),sQuery(id+"F0.wireOp",EDGE,"E21")])]});var subQ2=makeQuery(id+"F2.imprint","INTERSECT",VERTEX,{"disambiguationData":[OD(0.0)],"derivedFrom":[subQ1,subQ0]});Q93=makeQuery(id+"F2.imprint","IMPRINT",FACE,{"disambiguationData":[TD([[makeQuery(id+"F2.imprint","IMPRINT",EDGE,{"disambiguationData":[TD([[subQ2,-1.0]])],"derivedFrom":subQ0}),1.0]])]});}
            var Q94;
            {var subQ0=sQuery(id+"F2.wireOp",EDGE,"E23.36.0");var subQ1=makeQuery(id+"F1.opRevolve","SWEPT_EDGE",EDGE,{"disambiguationData":[OSD([sQuery(id+"F0.wireOp",EDGE,"E12"),sQuery(id+"F0.wireOp",EDGE,"E21")])]});var subQ2=makeQuery(id+"F2.imprint","INTERSECT",VERTEX,{"disambiguationData":[OD(0.0)],"derivedFrom":[subQ1,subQ0]});Q94=makeQuery(id+"F2.imprint","IMPRINT",FACE,{"disambiguationData":[TD([[makeQuery(id+"F2.imprint","IMPRINT",EDGE,{"disambiguationData":[TD([[subQ2,1.0]])],"derivedFrom":subQ0}),1.0]])]});}
            var Q95;
            {var subQ0=sQuery(id+"F2.wireOp",EDGE,"E23.36.0");var subQ1=makeQuery(id+"F1.opRevolve","SWEPT_EDGE",EDGE,{"disambiguationData":[OSD([sQuery(id+"F0.wireOp",EDGE,"E12"),sQuery(id+"F0.wireOp",EDGE,"E21")])]});var subQ2=makeQuery(id+"F2.imprint","INTERSECT",VERTEX,{"disambiguationData":[OD(0.0)],"derivedFrom":[subQ1,subQ0]});Q95=makeQuery(id+"F2.imprint","IMPRINT",FACE,{"disambiguationData":[TD([[makeQuery(id+"F2.imprint","IMPRINT",EDGE,{"disambiguationData":[TD([[subQ2,-1.0]])],"derivedFrom":subQ0}),1.0]])]});}
            var Q96;
            {var subQ0=sQuery(id+"F2.wireOp",EDGE,"E23.37.0");var subQ1=makeQuery(id+"F1.opRevolve","SWEPT_EDGE",EDGE,{"disambiguationData":[OSD([sQuery(id+"F0.wireOp",EDGE,"E12"),sQuery(id+"F0.wireOp",EDGE,"E21")])]});var subQ2=makeQuery(id+"F2.imprint","INTERSECT",VERTEX,{"disambiguationData":[OD(0.0)],"derivedFrom":[subQ1,subQ0]});Q96=makeQuery(id+"F2.imprint","IMPRINT",FACE,{"disambiguationData":[TD([[makeQuery(id+"F2.imprint","IMPRINT",EDGE,{"disambiguationData":[TD([[subQ2,-1.0]])],"derivedFrom":subQ0}),1.0]])]});}
            var Q97;
            {var subQ0=sQuery(id+"F2.wireOp",EDGE,"E23.37.0");var subQ1=makeQuery(id+"F1.opRevolve","SWEPT_EDGE",EDGE,{"disambiguationData":[OSD([sQuery(id+"F0.wireOp",EDGE,"E12"),sQuery(id+"F0.wireOp",EDGE,"E21")])]});var subQ2=makeQuery(id+"F2.imprint","INTERSECT",VERTEX,{"disambiguationData":[OD(0.0)],"derivedFrom":[subQ1,subQ0]});Q97=makeQuery(id+"F2.imprint","IMPRINT",FACE,{"disambiguationData":[TD([[makeQuery(id+"F2.imprint","IMPRINT",EDGE,{"disambiguationData":[TD([[subQ2,1.0]])],"derivedFrom":subQ0}),1.0]])]});}
            var Q98;
            {var subQ0=sQuery(id+"F2.wireOp",EDGE,"E23.38.0");var subQ1=makeQuery(id+"F1.opRevolve","SWEPT_EDGE",EDGE,{"disambiguationData":[OSD([sQuery(id+"F0.wireOp",EDGE,"E12"),sQuery(id+"F0.wireOp",EDGE,"E21")])]});var subQ2=makeQuery(id+"F2.imprint","INTERSECT",VERTEX,{"disambiguationData":[OD(0.0)],"derivedFrom":[subQ1,subQ0]});Q98=makeQuery(id+"F2.imprint","IMPRINT",FACE,{"disambiguationData":[TD([[makeQuery(id+"F2.imprint","IMPRINT",EDGE,{"disambiguationData":[TD([[subQ2,-1.0]])],"derivedFrom":subQ0}),1.0]])]});}
            var Q99;
            {var subQ0=sQuery(id+"F2.wireOp",EDGE,"E23.38.0");var subQ1=makeQuery(id+"F1.opRevolve","SWEPT_EDGE",EDGE,{"disambiguationData":[OSD([sQuery(id+"F0.wireOp",EDGE,"E12"),sQuery(id+"F0.wireOp",EDGE,"E21")])]});var subQ2=makeQuery(id+"F2.imprint","INTERSECT",VERTEX,{"disambiguationData":[OD(0.0)],"derivedFrom":[subQ1,subQ0]});Q99=makeQuery(id+"F2.imprint","IMPRINT",FACE,{"disambiguationData":[TD([[makeQuery(id+"F2.imprint","IMPRINT",EDGE,{"disambiguationData":[TD([[subQ2,1.0]])],"derivedFrom":subQ0}),1.0]])]});}
            var Q100;
            Q100=sQuery(id+"F2.wireOp",EDGE,"E23.46.0");
            extrude(context, id + "F3", {"entities" : qUnion([Q0, Q1, Q2, Q3, Q4, Q5, Q6, Q7, Q8, Q9, Q10, Q11, Q12, Q13, Q14, Q15, Q16, Q17, Q18, Q19, Q20, Q21, Q22, Q23, Q24, Q25, Q26, Q27, Q28, Q29, Q30, Q31, Q32, Q33, Q34, Q35, Q36, Q37, Q38, Q39, Q40, Q41, Q42, Q43, Q44, Q45, Q46, Q47, Q48, Q49, Q50, Q51, Q52, Q53, Q54, Q55, Q56, Q57, Q58, Q59, Q60, Q61, Q62, Q63, Q64, Q65, Q66, Q67, Q68, Q69, Q70, Q71, Q72, Q73, Q74, Q75, Q76, Q77, Q78, Q79, Q80, Q81, Q82, Q83, Q84, Q85, Q86, Q87, Q88, Q89, Q90, Q91, Q92, Q93, Q94, Q95, Q96, Q97, Q98, Q99]), "operationType" : NewBodyOperationType.ADD, "surfaceEntities" : qUnion([Q100]), "oppositeDirection" : true, "depth" : 97 * mm});
        }
        {
            var Q0;
            Q0=makeQuery(id+"F1.opRevolve","SWEPT_EDGE",EDGE,{"disambiguationData":[OSD([sQuery(id+"F0.wireOp",EDGE,"E8"),sQuery(id+"F0.wireOp",EDGE,"E9")])]});
            chamfer(context, id + "F4", {"entities" : qUnion([Q0]), "width" : 1 * mm, "tangentPropagation" : true});
        }
        {
            var Q0;
            Q0=qCreatedBy(makeId("Front.planeOp"),FACE);
            var sketch = newSketch(context, id + "F5", { "sketchPlane" : qUnion([Q0])});
            skLineSegment(sketch, "E24.bottom", {"start": v(0, 25.02) * mm, "end": v(-43.1, 25.02) * mm, "construction": true});
            skLineSegment(sketch, "E24.top", {"start": v(0, -7.37) * mm, "end": v(-43.1, -7.37) * mm, "construction": true});
            skLineSegment(sketch, "E24.left", {"start": v(0, 25.02) * mm, "end": v(0, -7.37) * mm, "construction": true});
            skLineSegment(sketch, "E24.right", {"start": v(-43.1, 25.02) * mm, "end": v(-43.1, -7.37) * mm, "construction": true});
            skLineSegment(sketch, "E25.bottom", {"start": v(-43.1, -7.37) * mm, "end": v(0, -7.37) * mm, "construction": true});
            skLineSegment(sketch, "E25.top", {"start": v(-43.1, -2.1) * mm, "end": v(0, -2.1) * mm, "construction": true});
            skLineSegment(sketch, "E25.left", {"start": v(-43.1, -7.37) * mm, "end": v(-43.1, -2.1) * mm, "construction": true});
            skLineSegment(sketch, "E25.right", {"start": v(0, -7.37) * mm, "end": v(0, -2.1) * mm, "construction": true});
            skLineSegment(sketch, "E26", {"start": v(0, -7.37) * mm, "end": v(-43.05, -7.37) * mm});
            skLineSegment(sketch, "E27", {"start": v(-43.05, -7.37) * mm, "end": v(-43.1, 24.63) * mm});
            skLineSegment(sketch, "E28", {"start": v(-43.1, 24.63) * mm, "end": v(-41.78, 24.63) * mm});
            skLineSegment(sketch, "E29", {"start": v(-41.78, 24.63) * mm, "end": v(-39.02, 21) * mm});
            skLineSegment(sketch, "E30", {"start": v(-39.02, 21) * mm, "end": v(-39, 14.8) * mm});
            skLineSegment(sketch, "E31", {"start": v(-39, 14.8) * mm, "end": v(-36.01, -2.03) * mm});
            skLineSegment(sketch, "E32", {"start": v(-36.01, -2.03) * mm, "end": v(0, -2.1) * mm});
            skLineSegment(sketch, "E33", {"start": v(0, -7.37) * mm, "end": v(0, -2.1) * mm});
            skPoint(sketch, "E34.oppositeSnap0", {"position": v(-40.4, 22.81) * mm});
            skLineSegment(sketch, "E34.bottom", {"start": v(-43.1, -4.73) * mm, "end": v(-45.35, -4.73) * mm});
            skLineSegment(sketch, "E34.top", {"start": v(-43.1, 22.81) * mm, "end": v(-45.35, 22.81) * mm});
            skLineSegment(sketch, "E34.left", {"start": v(-43.1, -4.73) * mm, "end": v(-43.1, 22.81) * mm});
            skLineSegment(sketch, "E34.right", {"start": v(-45.35, -4.73) * mm, "end": v(-45.35, 22.81) * mm});
            skSolve(sketch);
        }
        {
            var Q0;
            Q0=makeQuery(id+"F5.imprint","IMPRINT",FACE,{"disambiguationData":[TD([[makeQuery(id+"F5.imprint","IMPRINT",EDGE,{"derivedFrom":sQuery(id+"F5.wireOp",EDGE,"E26")}),-1.0]])]});
            var Q1;
            Q1=sQuery(id+"F5.wireOp",EDGE,"E33");
            revolve(context, id + "F6", {"entities" : qUnion([Q0]), "axis" : qUnion([Q1]), "revolveType" : RevolveType.FULL});
        }
        {
            var Q0;
            Q0=qCreatedBy(makeId("Front.planeOp"),FACE);
            var sketch = newSketch(context, id + "F7", { "sketchPlane" : qUnion([Q0])});
            skLineSegment(sketch, "E35.bottom", {"start": v(0, 24.6) * mm, "end": v(-44.5, 24.6) * mm, "construction": true});
            skLineSegment(sketch, "E35.top", {"start": v(0, -6.43) * mm, "end": v(-44.5, -6.43) * mm, "construction": true});
            skLineSegment(sketch, "E35.left", {"start": v(0, 24.6) * mm, "end": v(0, -6.43) * mm, "construction": true});
            skLineSegment(sketch, "E35.right", {"start": v(-44.5, 24.6) * mm, "end": v(-44.5, -6.43) * mm, "construction": true});
            skLineSegment(sketch, "E36", {"start": v(0, -6.43) * mm, "end": v(-42.95, -6.43) * mm});
            skLineSegment(sketch, "E37", {"start": v(-42.95, -6.43) * mm, "end": v(-44.5, -2.52) * mm});
            skLineSegment(sketch, "E38", {"start": v(-44.5, -2.52) * mm, "end": v(-44.5, 23.21) * mm});
            skLineSegment(sketch, "E39", {"start": v(-44.5, 23.21) * mm, "end": v(-42.01, 24.82) * mm});
            skLineSegment(sketch, "E40", {"start": v(-42.01, 24.82) * mm, "end": v(-39.04, 21) * mm});
            skLineSegment(sketch, "E41", {"start": v(-39.04, 21) * mm, "end": v(-39, 14.8) * mm});
            skLineSegment(sketch, "E42", {"start": v(-39, 14.8) * mm, "end": v(-36, -2.02) * mm});
            skLineSegment(sketch, "E43", {"start": v(-36, -2.02) * mm, "end": v(0, -2) * mm});
            skLineSegment(sketch, "E44", {"start": v(0, -2) * mm, "end": v(0, -6.43) * mm});
            skSolve(sketch);
        }
        {
            var Q0;
            Q0 = qSketchRegion(id + "F7", true);
            var Q1;
            Q1=sQuery(id+"F7.wireOp",EDGE,"E44");
            revolve(context, id + "F8", {"entities" : qUnion([Q0]), "axis" : qUnion([Q1]), "revolveType" : RevolveType.FULL});
        }
        {
            var Q0;
            Q0=qCreatedBy(makeId("Front.planeOp"),FACE);
            var sketch = newSketch(context, id + "F9", { "sketchPlane" : qUnion([Q0])});
            skLineSegment(sketch, "E45.bottom", {"start": v(0, 0) * mm, "end": v(-44.51, 0) * mm, "construction": true});
            skLineSegment(sketch, "E45.top", {"start": v(0, 27.4) * mm, "end": v(-44.51, 27.4) * mm, "construction": true});
            skLineSegment(sketch, "E45.left", {"start": v(0, 0) * mm, "end": v(0, 27.4) * mm, "construction": true});
            skLineSegment(sketch, "E45.right", {"start": v(-44.51, 0) * mm, "end": v(-44.51, 27.4) * mm, "construction": true});
            skLineSegment(sketch, "E46.bottom", {"start": v(-44.51, 27.4) * mm, "end": v(0, 27.4) * mm, "construction": true});
            skLineSegment(sketch, "E46.top", {"start": v(-44.51, 146.37) * mm, "end": v(0, 146.37) * mm, "construction": true});
            skLineSegment(sketch, "E46.left", {"start": v(-44.51, 27.4) * mm, "end": v(-44.51, 146.37) * mm, "construction": true});
            skLineSegment(sketch, "E46.right", {"start": v(0, 27.4) * mm, "end": v(0, 146.37) * mm, "construction": true});
            skLineSegment(sketch, "E47", {"start": v(0, 133.01) * mm, "end": v(-42.1, 133.01) * mm, "construction": true});
            skLineSegment(sketch, "E48", {"start": v(-42.1, 133.01) * mm, "end": v(-44.51, 129.97) * mm, "construction": true});
            skLineSegment(sketch, "E49", {"start": v(-44.51, 129.97) * mm, "end": v(-44.51, 123.64) * mm, "construction": true});
            skLineSegment(sketch, "E50", {"start": v(0, 133.01) * mm, "end": v(-42.1, 133.01) * mm});
            skLineSegment(sketch, "E51", {"start": v(-42.1, 133.01) * mm, "end": v(-44.51, 129.97) * mm});
            skLineSegment(sketch, "E52", {"start": v(-44.51, 129.97) * mm, "end": v(-44.51, 123.64) * mm});
            skLineSegment(sketch, "E53", {"start": v(0, 133.01) * mm, "end": v(0, 130.08) * mm});
            skLineSegment(sketch, "E54", {"start": v(0, 130.08) * mm, "end": v(-41.05, 130.08) * mm});
            skLineSegment(sketch, "E55", {"start": v(-41.05, 130.08) * mm, "end": v(-42.05, 129) * mm});
            skLineSegment(sketch, "E56", {"start": v(-42.05, 129) * mm, "end": v(-42.05, 123.99) * mm});
            skLineSegment(sketch, "E57", {"start": v(-42.05, 123.99) * mm, "end": v(-41.44, 122.02) * mm});
            skLineSegment(sketch, "E58", {"start": v(-41.44, 122.02) * mm, "end": v(-44.1, 122.02) * mm});
            skLineSegment(sketch, "E59", {"start": v(-44.1, 122.02) * mm, "end": v(-44.51, 123.64) * mm});
            skSolve(sketch);
        }
        {
            var Q0;
            Q0 = qSketchRegion(id + "F9", true);
            var Q1;
            Q1=sQuery(id+"F9.wireOp",EDGE,"E53");
            revolve(context, id + "F10", {"entities" : qUnion([Q0]), "axis" : qUnion([Q1]), "revolveType" : RevolveType.FULL});
        }
    });
